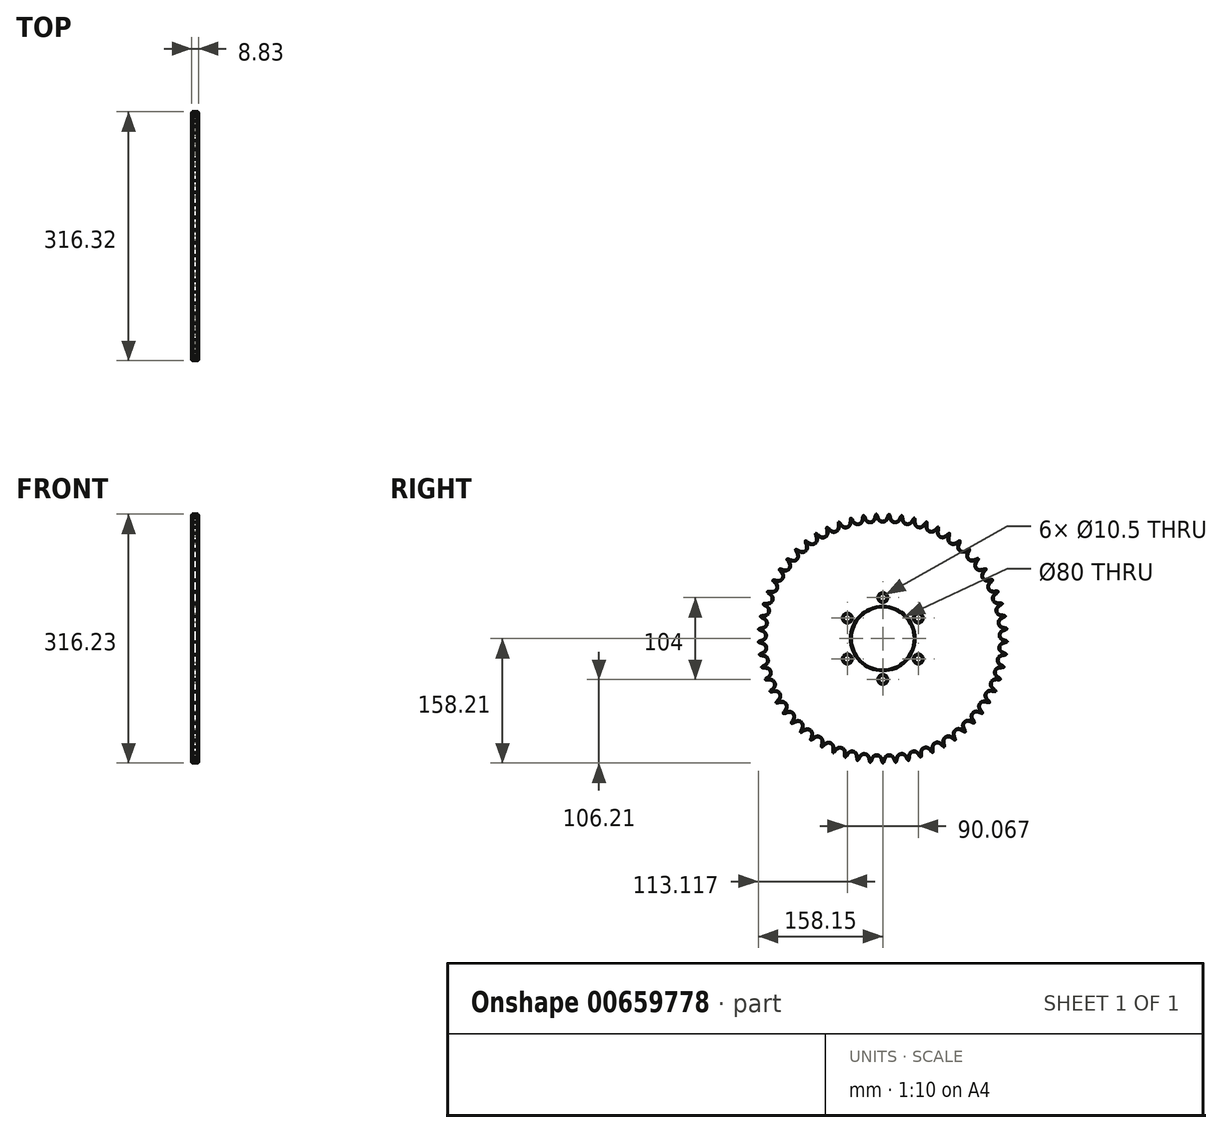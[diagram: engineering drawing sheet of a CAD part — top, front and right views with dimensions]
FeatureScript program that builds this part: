
annotation { "Feature Type Name" : "Feature", "Feature Type Description" : "" }
export const myFeature = defineFeature(function(context is Context, id is Id, definition is map)
    precondition{}
    {
        {
            var Q0;
            Q0=qCreatedBy(makeId("Front.planeOp"),FACE);
            var sketch = newSketch(context, id + "F0", { "sketchPlane" : qUnion([Q0])});
            skLineSegment(sketch, "E0", {"start": v(0, 0) * mm, "end": v(26.72, 0) * mm, "construction": true});
            skLineSegment(sketch, "E1.bottom", {"start": v(0, 40) * mm, "end": v(8.83, 40) * mm});
            skLineSegment(sketch, "E1.top", {"start": v(0, 158.2) * mm, "end": v(8.83, 158.2) * mm});
            skLineSegment(sketch, "E1.left", {"start": v(0, 40) * mm, "end": v(0, 158.2) * mm});
            skLineSegment(sketch, "E1.right", {"start": v(8.83, 40) * mm, "end": v(8.82, 158.2) * mm});
            skLineSegment(sketch, "E2.MirrorCS", {"start": v(8.83, -40) * mm, "end": v(8.83, -158.2) * mm});
            skLineSegment(sketch, "E3.MirrorCS", {"start": v(0, -158.2) * mm, "end": v(8.83, -158.2) * mm});
            skLineSegment(sketch, "E4.MirrorCS", {"start": v(0, -40) * mm, "end": v(8.83, -40) * mm});
            skLineSegment(sketch, "E5.MirrorCS", {"start": v(0, -40) * mm, "end": v(0, -158.2) * mm});
            skSolve(sketch);
        }
        {
            var Q0;
            Q0=makeQuery(id+"F0.imprint","IMPRINT",FACE,{"disambiguationData":[TD([[makeQuery(id+"F0.imprint","IMPRINT",EDGE,{"derivedFrom":sQuery(id+"F0.wireOp",EDGE,"E1.bottom")}),1.0]])]});
            var Q1;
            Q1=sQuery(id+"F0.wireOp",EDGE,"E0");
            revolve(context, id + "F1", {"entities" : qUnion([Q0]), "axis" : qUnion([Q1]), "revolveType" : RevolveType.FULL});
        }
        {
            var Q0;
            Q0=makeQuery(id+"F1.opRevolve","SWEPT_FACE",FACE,{"disambiguationData":[OSD([sQuery(id+"F0.wireOp",EDGE,"E1.left")])]});
            var sketch = newSketch(context, id + "F2", { "sketchPlane" : qUnion([Q0])});
            skCircle(sketch, "E6", {"center": v(0.24, 0) * mm, "radius": 158.2 * mm, "construction": true});
            skCircle(sketch, "E7", {"center": v(0.24, 0) * mm, "radius": 154.2 * mm, "construction": true});
            skCircle(sketch, "E8", {"center": v(0.24, 0) * mm, "radius": 149.03 * mm, "construction": true});
            skLineSegment(sketch, "E9", {"start": v(0.24, 0) * mm, "end": v(0.24, 107.73) * mm, "construction": true});
            skLineSegment(sketch, "E10", {"start": v(-4.24, 86.97) * mm, "end": v(0.24, 0) * mm, "construction": true});
            skLineSegment(sketch, "E11", {"start": v(0, 0) * mm, "end": v(0, 107.73) * mm, "construction": true});
            skLineSegment(sketch, "E12", {"start": v(0, 154.19) * mm, "end": v(-70.6, 102.92) * mm, "construction": true});
            skLineSegment(sketch, "E13", {"start": v(0, 154.19) * mm, "end": v(6.58, 158.97) * mm, "construction": true});
            skLineSegment(sketch, "E14", {"start": v(6.58, 158.97) * mm, "end": v(-48.08, 140.25) * mm, "construction": true});
            skLineSegment(sketch, "E15", {"start": v(-5.99, 154.66) * mm, "end": v(-6.34, 155.68) * mm});
            skLineSegment(sketch, "E16", {"start": v(-6.34, 155.68) * mm, "end": v(-12.58, 153.54) * mm, "construction": true});
            skArc(sketch, "E17", {"start": v(-5.99, 154.66) * mm, "mid": v(-5.21, 152.84) * mm, "end": v(-4.17, 151.16) * mm});
            skArc(sketch, "E18", {"start": v(-4.17, 151.16) * mm, "mid": v(18.37, 165.09) * mm, "end": v(-5.99, 154.66) * mm, "construction": true});
            skArc(sketch, "E19", {"start": v(0, 149.03) * mm, "mid": v(2.34, 158.78) * mm, "end": v(-4.17, 151.16) * mm, "construction": true});
            skArc(sketch, "E20", {"start": v(-4.17, 151.16) * mm, "mid": v(-2.34, 149.6) * mm, "end": v(0, 149.03) * mm});
            skLineSegment(sketch, "E21", {"start": v(0, 149.03) * mm, "end": v(0.24, 149.03) * mm});
            skArc(sketch, "E22", {"start": v(-7.92, 158.21) * mm, "mid": v(-18.18, 150.05) * mm, "end": v(-6.34, 155.68) * mm, "construction": true});
            skArc(sketch, "E23", {"start": v(-6.34, 155.68) * mm, "mid": v(-6.98, 157.04) * mm, "end": v(-7.92, 158.21) * mm});
            skArc(sketch, "E24.MirrorCS", {"start": v(4.65, 151.16) * mm, "mid": v(2.82, 149.6) * mm, "end": v(0.48, 149.03) * mm});
            skArc(sketch, "E25.MirrorCS", {"start": v(6.47, 154.66) * mm, "mid": v(5.69, 152.84) * mm, "end": v(4.65, 151.16) * mm});
            skLineSegment(sketch, "E26.MirrorCS", {"start": v(6.47, 154.66) * mm, "end": v(6.81, 155.68) * mm});
            skArc(sketch, "E27.MirrorCS", {"start": v(6.81, 155.68) * mm, "mid": v(7.46, 157.04) * mm, "end": v(8.4, 158.21) * mm});
            skLineSegment(sketch, "E28.MirrorCS", {"start": v(0.48, 149.03) * mm, "end": v(0.24, 149.03) * mm});
            skArc(sketch, "E29.1.0", {"start": v(-22.31, 154.2) * mm, "mid": v(-23.1, 155.49) * mm, "end": v(-24.14, 156.56) * mm});
            skArc(sketch, "E29.1.1", {"start": v(-9.23, 155.56) * mm, "mid": v(-8.73, 156.97) * mm, "end": v(-7.92, 158.23) * mm});
            skLineSegment(sketch, "E29.1.2", {"start": v(-9.47, 154.5) * mm, "end": v(-9.23, 155.56) * mm});
            skArc(sketch, "E29.1.3", {"start": v(-9.47, 154.5) * mm, "mid": v(-10.06, 152.62) * mm, "end": v(-10.92, 150.84) * mm});
            skArc(sketch, "E29.1.4", {"start": v(-10.92, 150.84) * mm, "mid": v(-12.58, 149.1) * mm, "end": v(-14.85, 148.3) * mm});
            skArc(sketch, "E29.1.5", {"start": v(-19.7, 149.93) * mm, "mid": v(-17.71, 148.56) * mm, "end": v(-15.32, 148.24) * mm});
            skArc(sketch, "E29.1.6", {"start": v(-21.86, 153.23) * mm, "mid": v(-20.9, 151.5) * mm, "end": v(-19.7, 149.93) * mm});
            skLineSegment(sketch, "E29.1.7", {"start": v(-21.86, 153.23) * mm, "end": v(-22.31, 154.2) * mm});
            skLineSegment(sketch, "E29.1.8", {"start": v(-14.85, 148.3) * mm, "end": v(-15.09, 148.27) * mm});
            skLineSegment(sketch, "E29.1.9", {"start": v(-15.32, 148.24) * mm, "end": v(-15.09, 148.27) * mm});
            skArc(sketch, "E29.2.0", {"start": v(-38.05, 151.1) * mm, "mid": v(-38.96, 152.29) * mm, "end": v(-40.11, 153.25) * mm});
            skArc(sketch, "E29.2.1", {"start": v(-25.17, 153.78) * mm, "mid": v(-24.82, 155.24) * mm, "end": v(-24.15, 156.58) * mm});
            skLineSegment(sketch, "E29.2.2", {"start": v(-25.3, 152.71) * mm, "end": v(-25.17, 153.78) * mm});
            skArc(sketch, "E29.2.3", {"start": v(-25.3, 152.71) * mm, "mid": v(-25.7, 150.78) * mm, "end": v(-26.37, 148.92) * mm});
            skArc(sketch, "E29.2.4", {"start": v(-26.37, 148.92) * mm, "mid": v(-27.84, 147.01) * mm, "end": v(-30.02, 145.98) * mm});
            skArc(sketch, "E29.2.5", {"start": v(-35, 147.11) * mm, "mid": v(-32.9, 145.96) * mm, "end": v(-30.49, 145.88) * mm});
            skArc(sketch, "E29.2.6", {"start": v(-37.5, 150.17) * mm, "mid": v(-36.37, 148.55) * mm, "end": v(-35, 147.11) * mm});
            skLineSegment(sketch, "E29.2.7", {"start": v(-37.5, 150.17) * mm, "end": v(-38.05, 151.1) * mm});
            skLineSegment(sketch, "E29.2.8", {"start": v(-30.02, 145.98) * mm, "end": v(-30.25, 145.93) * mm});
            skLineSegment(sketch, "E29.2.9", {"start": v(-30.49, 145.88) * mm, "end": v(-30.25, 145.93) * mm});
            skArc(sketch, "E29.3.0", {"start": v(-53.38, 146.38) * mm, "mid": v(-54.4, 147.47) * mm, "end": v(-55.66, 148.3) * mm});
            skArc(sketch, "E29.3.1", {"start": v(-40.85, 150.38) * mm, "mid": v(-40.65, 151.87) * mm, "end": v(-40.12, 153.27) * mm});
            skLineSegment(sketch, "E29.3.2", {"start": v(-40.88, 149.3) * mm, "end": v(-40.85, 150.38) * mm});
            skArc(sketch, "E29.3.3", {"start": v(-40.88, 149.3) * mm, "mid": v(-41.06, 147.33) * mm, "end": v(-41.54, 145.41) * mm});
            skArc(sketch, "E29.3.4", {"start": v(-41.54, 145.41) * mm, "mid": v(-42.81, 143.37) * mm, "end": v(-44.87, 142.12) * mm});
            skArc(sketch, "E29.3.5", {"start": v(-49.94, 142.73) * mm, "mid": v(-47.72, 141.8) * mm, "end": v(-45.32, 141.98) * mm});
            skArc(sketch, "E29.3.6", {"start": v(-52.74, 145.52) * mm, "mid": v(-51.45, 144.02) * mm, "end": v(-49.94, 142.73) * mm});
            skLineSegment(sketch, "E29.3.7", {"start": v(-52.74, 145.52) * mm, "end": v(-53.38, 146.38) * mm});
            skLineSegment(sketch, "E29.3.8", {"start": v(-44.87, 142.12) * mm, "end": v(-45.1, 142.05) * mm});
            skLineSegment(sketch, "E29.3.9", {"start": v(-45.32, 141.98) * mm, "end": v(-45.1, 142.05) * mm});
            skArc(sketch, "E29.4.0", {"start": v(-68.15, 140.11) * mm, "mid": v(-69.28, 141.1) * mm, "end": v(-70.61, 141.8) * mm});
            skArc(sketch, "E29.4.1", {"start": v(-56.1, 145.38) * mm, "mid": v(-56.05, 146.88) * mm, "end": v(-55.67, 148.33) * mm});
            skLineSegment(sketch, "E29.4.2", {"start": v(-56.01, 144.3) * mm, "end": v(-56.1, 145.38) * mm});
            skArc(sketch, "E29.4.3", {"start": v(-56.01, 144.3) * mm, "mid": v(-56, 142.33) * mm, "end": v(-56.27, 140.37) * mm});
            skArc(sketch, "E29.4.4", {"start": v(-56.27, 140.37) * mm, "mid": v(-57.33, 138.2) * mm, "end": v(-59.25, 136.75) * mm});
            skArc(sketch, "E29.4.5", {"start": v(-64.36, 136.84) * mm, "mid": v(-62.05, 136.14) * mm, "end": v(-59.68, 136.56) * mm});
            skArc(sketch, "E29.4.6", {"start": v(-67.42, 139.32) * mm, "mid": v(-65.98, 137.97) * mm, "end": v(-64.36, 136.84) * mm});
            skLineSegment(sketch, "E29.4.7", {"start": v(-67.42, 139.32) * mm, "end": v(-68.15, 140.11) * mm});
            skLineSegment(sketch, "E29.4.8", {"start": v(-59.25, 136.75) * mm, "end": v(-59.46, 136.66) * mm});
            skLineSegment(sketch, "E29.4.9", {"start": v(-59.68, 136.56) * mm, "end": v(-59.46, 136.66) * mm});
            skArc(sketch, "E29.5.0", {"start": v(-82.2, 132.36) * mm, "mid": v(-83.42, 133.23) * mm, "end": v(-84.82, 133.79) * mm});
            skArc(sketch, "E29.5.1", {"start": v(-70.75, 138.84) * mm, "mid": v(-70.86, 140.34) * mm, "end": v(-70.62, 141.82) * mm});
            skLineSegment(sketch, "E29.5.2", {"start": v(-70.55, 137.79) * mm, "end": v(-70.75, 138.84) * mm});
            skArc(sketch, "E29.5.3", {"start": v(-70.55, 137.79) * mm, "mid": v(-70.33, 135.82) * mm, "end": v(-70.4, 133.84) * mm});
            skArc(sketch, "E29.5.4", {"start": v(-70.4, 133.84) * mm, "mid": v(-71.23, 131.58) * mm, "end": v(-73, 129.94) * mm});
            skArc(sketch, "E29.5.5", {"start": v(-78.08, 129.5) * mm, "mid": v(-75.72, 129.04) * mm, "end": v(-73.4, 129.7) * mm});
            skArc(sketch, "E29.5.6", {"start": v(-81.4, 131.65) * mm, "mid": v(-79.82, 130.45) * mm, "end": v(-78.08, 129.5) * mm});
            skLineSegment(sketch, "E29.5.7", {"start": v(-81.4, 131.65) * mm, "end": v(-82.2, 132.36) * mm});
            skLineSegment(sketch, "E29.5.8", {"start": v(-73, 129.94) * mm, "end": v(-73.2, 129.82) * mm});
            skLineSegment(sketch, "E29.5.9", {"start": v(-73.4, 129.7) * mm, "end": v(-73.2, 129.82) * mm});
            skArc(sketch, "E29.6.0", {"start": v(-95.37, 123.21) * mm, "mid": v(-96.68, 123.94) * mm, "end": v(-98.12, 124.36) * mm});
            skArc(sketch, "E29.6.1", {"start": v(-84.65, 130.83) * mm, "mid": v(-84.91, 132.31) * mm, "end": v(-84.83, 133.8) * mm});
            skLineSegment(sketch, "E29.6.2", {"start": v(-84.35, 129.8) * mm, "end": v(-84.65, 130.83) * mm});
            skArc(sketch, "E29.6.3", {"start": v(-84.35, 129.8) * mm, "mid": v(-83.93, 127.87) * mm, "end": v(-83.8, 125.9) * mm});
            skArc(sketch, "E29.6.4", {"start": v(-83.8, 125.9) * mm, "mid": v(-84.38, 123.56) * mm, "end": v(-85.97, 121.74) * mm});
            skArc(sketch, "E29.6.5", {"start": v(-90.99, 120.78) * mm, "mid": v(-88.59, 120.57) * mm, "end": v(-86.35, 121.47) * mm});
            skArc(sketch, "E29.6.6", {"start": v(-94.5, 122.58) * mm, "mid": v(-92.8, 121.55) * mm, "end": v(-90.99, 120.78) * mm});
            skLineSegment(sketch, "E29.6.7", {"start": v(-94.5, 122.58) * mm, "end": v(-95.37, 123.21) * mm});
            skLineSegment(sketch, "E29.6.8", {"start": v(-85.97, 121.74) * mm, "end": v(-86.16, 121.6) * mm});
            skLineSegment(sketch, "E29.6.9", {"start": v(-86.35, 121.47) * mm, "end": v(-86.16, 121.6) * mm});
            skArc(sketch, "E29.7.0", {"start": v(-107.53, 112.75) * mm, "mid": v(-108.91, 113.34) * mm, "end": v(-110.39, 113.61) * mm});
            skArc(sketch, "E29.7.1", {"start": v(-97.65, 121.43) * mm, "mid": v(-98.06, 122.88) * mm, "end": v(-98.14, 124.38) * mm});
            skLineSegment(sketch, "E29.7.2", {"start": v(-97.24, 120.44) * mm, "end": v(-97.65, 121.43) * mm});
            skArc(sketch, "E29.7.3", {"start": v(-97.24, 120.44) * mm, "mid": v(-96.63, 118.56) * mm, "end": v(-96.3, 116.6) * mm});
            skArc(sketch, "E29.7.4", {"start": v(-96.3, 116.6) * mm, "mid": v(-96.64, 114.23) * mm, "end": v(-98.03, 112.26) * mm});
            skArc(sketch, "E29.7.5", {"start": v(-102.92, 110.79) * mm, "mid": v(-100.52, 110.82) * mm, "end": v(-98.39, 111.94) * mm});
            skArc(sketch, "E29.7.6", {"start": v(-106.6, 112.22) * mm, "mid": v(-104.81, 111.37) * mm, "end": v(-102.92, 110.79) * mm});
            skLineSegment(sketch, "E29.7.7", {"start": v(-106.6, 112.22) * mm, "end": v(-107.53, 112.75) * mm});
            skLineSegment(sketch, "E29.7.8", {"start": v(-98.03, 112.26) * mm, "end": v(-98.2, 112.1) * mm});
            skLineSegment(sketch, "E29.7.9", {"start": v(-98.39, 111.94) * mm, "end": v(-98.2, 112.1) * mm});
            skArc(sketch, "E29.8.0", {"start": v(-118.56, 101.1) * mm, "mid": v(-119.99, 101.55) * mm, "end": v(-121.49, 101.66) * mm});
            skArc(sketch, "E29.8.1", {"start": v(-109.62, 110.75) * mm, "mid": v(-110.18, 112.14) * mm, "end": v(-110.4, 113.63) * mm});
            skLineSegment(sketch, "E29.8.2", {"start": v(-109.11, 109.8) * mm, "end": v(-109.62, 110.75) * mm});
            skArc(sketch, "E29.8.3", {"start": v(-109.11, 109.8) * mm, "mid": v(-108.3, 108) * mm, "end": v(-107.78, 106.1) * mm});
            skArc(sketch, "E29.8.4", {"start": v(-107.78, 106.1) * mm, "mid": v(-107.87, 103.68) * mm, "end": v(-109.05, 101.58) * mm});
            skArc(sketch, "E29.8.5", {"start": v(-113.77, 99.62) * mm, "mid": v(-111.38, 99.9) * mm, "end": v(-109.37, 101.24) * mm});
            skArc(sketch, "E29.8.6", {"start": v(-117.57, 100.66) * mm, "mid": v(-115.7, 100) * mm, "end": v(-113.77, 99.62) * mm});
            skLineSegment(sketch, "E29.8.7", {"start": v(-117.57, 100.66) * mm, "end": v(-118.56, 101.1) * mm});
            skLineSegment(sketch, "E29.8.8", {"start": v(-109.05, 101.58) * mm, "end": v(-109.21, 101.41) * mm});
            skLineSegment(sketch, "E29.8.9", {"start": v(-109.37, 101.24) * mm, "end": v(-109.21, 101.41) * mm});
            skArc(sketch, "E29.9.0", {"start": v(-128.32, 88.37) * mm, "mid": v(-129.8, 88.67) * mm, "end": v(-131.3, 88.63) * mm});
            skArc(sketch, "E29.9.1", {"start": v(-120.43, 98.9) * mm, "mid": v(-121.13, 100.22) * mm, "end": v(-121.5, 101.67) * mm});
            skLineSegment(sketch, "E29.9.2", {"start": v(-119.82, 98) * mm, "end": v(-120.43, 98.9) * mm});
            skArc(sketch, "E29.9.3", {"start": v(-119.82, 98) * mm, "mid": v(-118.84, 96.29) * mm, "end": v(-118.12, 94.45) * mm});
            skArc(sketch, "E29.9.4", {"start": v(-118.12, 94.45) * mm, "mid": v(-117.96, 92.04) * mm, "end": v(-118.92, 89.83) * mm});
            skArc(sketch, "E29.9.5", {"start": v(-123.4, 87.4) * mm, "mid": v(-121.06, 87.92) * mm, "end": v(-119.2, 89.45) * mm});
            skArc(sketch, "E29.9.6", {"start": v(-127.3, 88.04) * mm, "mid": v(-125.38, 87.57) * mm, "end": v(-123.4, 87.4) * mm});
            skLineSegment(sketch, "E29.9.7", {"start": v(-127.3, 88.04) * mm, "end": v(-128.32, 88.37) * mm});
            skLineSegment(sketch, "E29.9.8", {"start": v(-118.92, 89.83) * mm, "end": v(-119.06, 89.64) * mm});
            skLineSegment(sketch, "E29.9.9", {"start": v(-119.2, 89.45) * mm, "end": v(-119.06, 89.64) * mm});
            skArc(sketch, "E29.10.0", {"start": v(-136.73, 74.7) * mm, "mid": v(-138.22, 74.85) * mm, "end": v(-139.71, 74.66) * mm});
            skArc(sketch, "E29.10.1", {"start": v(-129.96, 85.98) * mm, "mid": v(-130.79, 87.24) * mm, "end": v(-131.32, 88.64) * mm});
            skLineSegment(sketch, "E29.10.2", {"start": v(-129.27, 85.16) * mm, "end": v(-129.96, 85.98) * mm});
            skArc(sketch, "E29.10.3", {"start": v(-129.27, 85.16) * mm, "mid": v(-128.1, 83.56) * mm, "end": v(-127.2, 81.8) * mm});
            skArc(sketch, "E29.10.4", {"start": v(-127.2, 81.8) * mm, "mid": v(-126.8, 79.43) * mm, "end": v(-127.52, 77.13) * mm});
            skArc(sketch, "E29.10.5", {"start": v(-131.74, 74.24) * mm, "mid": v(-129.46, 75) * mm, "end": v(-127.77, 76.72) * mm});
            skArc(sketch, "E29.10.6", {"start": v(-135.68, 74.48) * mm, "mid": v(-133.72, 74.22) * mm, "end": v(-131.74, 74.24) * mm});
            skLineSegment(sketch, "E29.10.7", {"start": v(-135.68, 74.48) * mm, "end": v(-136.73, 74.7) * mm});
            skLineSegment(sketch, "E29.10.8", {"start": v(-127.52, 77.13) * mm, "end": v(-127.65, 76.93) * mm});
            skLineSegment(sketch, "E29.10.9", {"start": v(-127.77, 76.72) * mm, "end": v(-127.65, 76.93) * mm});
            skArc(sketch, "E29.11.0", {"start": v(-143.69, 60.25) * mm, "mid": v(-145.19, 60.25) * mm, "end": v(-146.65, 59.9) * mm});
            skArc(sketch, "E29.11.1", {"start": v(-138.11, 72.17) * mm, "mid": v(-139.07, 73.32) * mm, "end": v(-139.73, 74.67) * mm});
            skLineSegment(sketch, "E29.11.2", {"start": v(-137.34, 71.42) * mm, "end": v(-138.11, 72.17) * mm});
            skArc(sketch, "E29.11.3", {"start": v(-137.34, 71.42) * mm, "mid": v(-136.02, 69.94) * mm, "end": v(-134.94, 68.29) * mm});
            skArc(sketch, "E29.11.4", {"start": v(-134.94, 68.29) * mm, "mid": v(-134.3, 65.97) * mm, "end": v(-134.78, 63.6) * mm});
            skArc(sketch, "E29.11.5", {"start": v(-138.68, 60.3) * mm, "mid": v(-136.48, 61.3) * mm, "end": v(-134.98, 63.18) * mm});
            skArc(sketch, "E29.11.6", {"start": v(-142.62, 60.14) * mm, "mid": v(-140.64, 60.07) * mm, "end": v(-138.68, 60.3) * mm});
            skLineSegment(sketch, "E29.11.7", {"start": v(-142.62, 60.14) * mm, "end": v(-143.69, 60.25) * mm});
            skLineSegment(sketch, "E29.11.8", {"start": v(-134.78, 63.6) * mm, "end": v(-134.88, 63.4) * mm});
            skLineSegment(sketch, "E29.11.9", {"start": v(-134.98, 63.18) * mm, "end": v(-134.88, 63.4) * mm});
            skArc(sketch, "E29.12.0", {"start": v(-149.12, 45.16) * mm, "mid": v(-150.61, 45) * mm, "end": v(-152.03, 44.5) * mm});
            skArc(sketch, "E29.12.1", {"start": v(-144.8, 57.58) * mm, "mid": v(-145.87, 58.64) * mm, "end": v(-146.67, 59.9) * mm});
            skLineSegment(sketch, "E29.12.2", {"start": v(-143.95, 56.92) * mm, "end": v(-144.8, 57.58) * mm});
            skArc(sketch, "E29.12.3", {"start": v(-143.95, 56.92) * mm, "mid": v(-142.5, 55.59) * mm, "end": v(-141.24, 54.05) * mm});
            skArc(sketch, "E29.12.4", {"start": v(-141.24, 54.05) * mm, "mid": v(-140.37, 51.8) * mm, "end": v(-140.6, 49.41) * mm});
            skArc(sketch, "E29.12.5", {"start": v(-144.14, 45.72) * mm, "mid": v(-142.06, 46.94) * mm, "end": v(-140.76, 48.96) * mm});
            skArc(sketch, "E29.12.6", {"start": v(-148.04, 45.16) * mm, "mid": v(-146.07, 45.3) * mm, "end": v(-144.14, 45.72) * mm});
            skLineSegment(sketch, "E29.12.7", {"start": v(-148.04, 45.16) * mm, "end": v(-149.12, 45.16) * mm});
            skLineSegment(sketch, "E29.12.8", {"start": v(-140.6, 49.41) * mm, "end": v(-140.68, 49.19) * mm});
            skLineSegment(sketch, "E29.12.9", {"start": v(-140.76, 48.96) * mm, "end": v(-140.68, 49.19) * mm});
            skArc(sketch, "E29.13.0", {"start": v(-152.97, 29.59) * mm, "mid": v(-154.44, 29.27) * mm, "end": v(-155.8, 28.63) * mm});
            skArc(sketch, "E29.13.1", {"start": v(-149.95, 42.39) * mm, "mid": v(-151.12, 43.33) * mm, "end": v(-152.05, 44.5) * mm});
            skLineSegment(sketch, "E29.13.2", {"start": v(-149.04, 41.82) * mm, "end": v(-149.95, 42.39) * mm});
            skArc(sketch, "E29.13.3", {"start": v(-149.04, 41.82) * mm, "mid": v(-147.45, 40.64) * mm, "end": v(-146.05, 39.24) * mm});
            skArc(sketch, "E29.13.4", {"start": v(-146.05, 39.24) * mm, "mid": v(-144.95, 37.1) * mm, "end": v(-144.94, 34.7) * mm});
            skArc(sketch, "E29.13.5", {"start": v(-148.08, 30.66) * mm, "mid": v(-146.14, 32.08) * mm, "end": v(-145.05, 34.23) * mm});
            skArc(sketch, "E29.13.6", {"start": v(-151.9, 29.7) * mm, "mid": v(-149.95, 30.03) * mm, "end": v(-148.08, 30.66) * mm});
            skLineSegment(sketch, "E29.13.7", {"start": v(-151.9, 29.7) * mm, "end": v(-152.97, 29.59) * mm});
            skLineSegment(sketch, "E29.13.8", {"start": v(-144.94, 34.7) * mm, "end": v(-145, 34.46) * mm});
            skLineSegment(sketch, "E29.13.9", {"start": v(-145.05, 34.23) * mm, "end": v(-145, 34.46) * mm});
            skArc(sketch, "E29.14.0", {"start": v(-155.2, 13.7) * mm, "mid": v(-156.63, 13.24) * mm, "end": v(-157.92, 12.46) * mm});
            skArc(sketch, "E29.14.1", {"start": v(-153.52, 26.75) * mm, "mid": v(-154.78, 27.56) * mm, "end": v(-155.82, 28.64) * mm});
            skLineSegment(sketch, "E29.14.2", {"start": v(-152.55, 26.27) * mm, "end": v(-153.52, 26.75) * mm});
            skArc(sketch, "E29.14.3", {"start": v(-152.55, 26.27) * mm, "mid": v(-150.85, 25.27) * mm, "end": v(-149.31, 24.02) * mm});
            skArc(sketch, "E29.14.4", {"start": v(-149.31, 24.02) * mm, "mid": v(-148, 22) * mm, "end": v(-147.74, 19.6) * mm});
            skArc(sketch, "E29.14.5", {"start": v(-150.45, 15.27) * mm, "mid": v(-148.66, 16.89) * mm, "end": v(-147.8, 19.14) * mm});
            skArc(sketch, "E29.14.6", {"start": v(-154.15, 13.92) * mm, "mid": v(-152.25, 14.46) * mm, "end": v(-150.45, 15.27) * mm});
            skLineSegment(sketch, "E29.14.7", {"start": v(-154.15, 13.92) * mm, "end": v(-155.2, 13.7) * mm});
            skLineSegment(sketch, "E29.14.8", {"start": v(-147.74, 19.6) * mm, "end": v(-147.77, 19.37) * mm});
            skLineSegment(sketch, "E29.14.9", {"start": v(-147.8, 19.14) * mm, "end": v(-147.77, 19.37) * mm});
            skArc(sketch, "E29.15.0", {"start": v(-155.8, -2.33) * mm, "mid": v(-157.16, -2.94) * mm, "end": v(-158.36, -3.84) * mm});
            skArc(sketch, "E29.15.1", {"start": v(-155.45, 10.82) * mm, "mid": v(-156.8, 11.5) * mm, "end": v(-157.94, 12.46) * mm});
            skLineSegment(sketch, "E29.15.2", {"start": v(-154.44, 10.45) * mm, "end": v(-155.45, 10.82) * mm});
            skArc(sketch, "E29.15.3", {"start": v(-154.44, 10.45) * mm, "mid": v(-152.65, 9.62) * mm, "end": v(-151, 8.54) * mm});
            skArc(sketch, "E29.15.4", {"start": v(-151, 8.54) * mm, "mid": v(-149.47, 6.67) * mm, "end": v(-148.97, 4.31) * mm});
            skArc(sketch, "E29.15.5", {"start": v(-151.22, -0.28) * mm, "mid": v(-149.6, 1.51) * mm, "end": v(-148.99, 3.84) * mm});
            skArc(sketch, "E29.15.6", {"start": v(-154.77, -2) * mm, "mid": v(-152.93, -1.27) * mm, "end": v(-151.22, -0.28) * mm});
            skLineSegment(sketch, "E29.15.7", {"start": v(-154.77, -2) * mm, "end": v(-155.8, -2.33) * mm});
            skLineSegment(sketch, "E29.15.8", {"start": v(-148.97, 4.31) * mm, "end": v(-148.98, 4.08) * mm});
            skLineSegment(sketch, "E29.15.9", {"start": v(-148.99, 3.84) * mm, "end": v(-148.98, 4.08) * mm});
            skArc(sketch, "E29.16.0", {"start": v(-154.73, -18.33) * mm, "mid": v(-156.03, -19.08) * mm, "end": v(-157.13, -20.1) * mm});
            skArc(sketch, "E29.16.1", {"start": v(-155.74, -5.22) * mm, "mid": v(-157.14, -4.68) * mm, "end": v(-158.39, -3.84) * mm});
            skLineSegment(sketch, "E29.16.2", {"start": v(-154.7, -5.49) * mm, "end": v(-155.74, -5.22) * mm});
            skArc(sketch, "E29.16.3", {"start": v(-154.7, -5.49) * mm, "mid": v(-152.83, -6.13) * mm, "end": v(-151.07, -7.03) * mm});
            skArc(sketch, "E29.16.4", {"start": v(-151.07, -7.03) * mm, "mid": v(-149.37, -8.74) * mm, "end": v(-148.63, -11.03) * mm});
            skArc(sketch, "E29.16.5", {"start": v(-150.39, -15.82) * mm, "mid": v(-148.97, -13.88) * mm, "end": v(-148.6, -11.5) * mm});
            skArc(sketch, "E29.16.6", {"start": v(-153.74, -17.9) * mm, "mid": v(-151.99, -17) * mm, "end": v(-150.39, -15.82) * mm});
            skLineSegment(sketch, "E29.16.7", {"start": v(-153.74, -17.9) * mm, "end": v(-154.73, -18.33) * mm});
            skLineSegment(sketch, "E29.16.8", {"start": v(-148.63, -11.03) * mm, "end": v(-148.6, -11.26) * mm});
            skLineSegment(sketch, "E29.16.9", {"start": v(-148.6, -11.5) * mm, "end": v(-148.6, -11.26) * mm});
            skArc(sketch, "E29.17.0", {"start": v(-152.02, -34.15) * mm, "mid": v(-153.24, -35.02) * mm, "end": v(-154.23, -36.15) * mm});
            skArc(sketch, "E29.17.1", {"start": v(-154.38, -21.2) * mm, "mid": v(-155.83, -20.82) * mm, "end": v(-157.15, -20.1) * mm});
            skLineSegment(sketch, "E29.17.2", {"start": v(-153.32, -21.37) * mm, "end": v(-154.38, -21.2) * mm});
            skArc(sketch, "E29.17.3", {"start": v(-153.32, -21.37) * mm, "mid": v(-151.39, -21.8) * mm, "end": v(-149.55, -22.53) * mm});
            skArc(sketch, "E29.17.4", {"start": v(-149.55, -22.53) * mm, "mid": v(-147.68, -24.05) * mm, "end": v(-146.7, -26.25) * mm});
            skArc(sketch, "E29.17.5", {"start": v(-147.96, -31.2) * mm, "mid": v(-146.75, -29.12) * mm, "end": v(-146.62, -26.72) * mm});
            skArc(sketch, "E29.17.6", {"start": v(-151.08, -33.62) * mm, "mid": v(-149.43, -32.53) * mm, "end": v(-147.96, -31.2) * mm});
            skLineSegment(sketch, "E29.17.7", {"start": v(-151.08, -33.62) * mm, "end": v(-152.02, -34.15) * mm});
            skLineSegment(sketch, "E29.17.8", {"start": v(-146.7, -26.25) * mm, "end": v(-146.66, -26.48) * mm});
            skLineSegment(sketch, "E29.17.9", {"start": v(-146.62, -26.72) * mm, "end": v(-146.66, -26.48) * mm});
            skArc(sketch, "E29.18.0", {"start": v(-147.7, -49.6) * mm, "mid": v(-148.83, -50.6) * mm, "end": v(-149.7, -51.82) * mm});
            skArc(sketch, "E29.18.1", {"start": v(-151.38, -36.97) * mm, "mid": v(-152.86, -36.73) * mm, "end": v(-154.25, -36.16) * mm});
            skLineSegment(sketch, "E29.18.2", {"start": v(-150.3, -37.02) * mm, "end": v(-151.38, -36.97) * mm});
            skArc(sketch, "E29.18.3", {"start": v(-150.3, -37.02) * mm, "mid": v(-148.34, -37.26) * mm, "end": v(-146.44, -37.79) * mm});
            skArc(sketch, "E29.18.4", {"start": v(-146.44, -37.79) * mm, "mid": v(-144.42, -39.1) * mm, "end": v(-143.23, -41.2) * mm});
            skArc(sketch, "E29.18.5", {"start": v(-143.97, -46.25) * mm, "mid": v(-142.98, -44.06) * mm, "end": v(-143.1, -41.65) * mm});
            skArc(sketch, "E29.18.6", {"start": v(-146.83, -48.98) * mm, "mid": v(-145.3, -47.72) * mm, "end": v(-143.97, -46.25) * mm});
            skLineSegment(sketch, "E29.18.7", {"start": v(-146.83, -48.98) * mm, "end": v(-147.7, -49.6) * mm});
            skLineSegment(sketch, "E29.18.8", {"start": v(-143.23, -41.2) * mm, "end": v(-143.16, -41.42) * mm});
            skLineSegment(sketch, "E29.18.9", {"start": v(-143.1, -41.65) * mm, "end": v(-143.16, -41.42) * mm});
            skArc(sketch, "E29.19.0", {"start": v(-141.82, -64.52) * mm, "mid": v(-142.84, -65.63) * mm, "end": v(-143.57, -66.94) * mm});
            skArc(sketch, "E29.19.1", {"start": v(-146.78, -52.34) * mm, "mid": v(-148.28, -52.25) * mm, "end": v(-149.72, -51.83) * mm});
            skLineSegment(sketch, "E29.19.2", {"start": v(-145.7, -52.28) * mm, "end": v(-146.78, -52.34) * mm});
            skArc(sketch, "E29.19.3", {"start": v(-145.7, -52.28) * mm, "mid": v(-143.73, -52.31) * mm, "end": v(-141.77, -52.64) * mm});
            skArc(sketch, "E29.19.4", {"start": v(-141.77, -52.64) * mm, "mid": v(-139.64, -53.75) * mm, "end": v(-138.23, -55.7) * mm});
            skArc(sketch, "E29.19.5", {"start": v(-138.45, -60.81) * mm, "mid": v(-137.7, -58.53) * mm, "end": v(-138.05, -56.15) * mm});
            skArc(sketch, "E29.19.6", {"start": v(-141.01, -63.81) * mm, "mid": v(-139.62, -62.4) * mm, "end": v(-138.45, -60.81) * mm});
            skLineSegment(sketch, "E29.19.7", {"start": v(-141.01, -63.81) * mm, "end": v(-141.82, -64.52) * mm});
            skLineSegment(sketch, "E29.19.8", {"start": v(-138.23, -55.7) * mm, "end": v(-138.14, -55.93) * mm});
            skLineSegment(sketch, "E29.19.9", {"start": v(-138.05, -56.15) * mm, "end": v(-138.14, -55.93) * mm});
            skArc(sketch, "E29.20.0", {"start": v(-134.44, -78.76) * mm, "mid": v(-135.33, -79.97) * mm, "end": v(-135.93, -81.34) * mm});
            skArc(sketch, "E29.20.1", {"start": v(-140.62, -67.15) * mm, "mid": v(-142.12, -67.22) * mm, "end": v(-143.6, -66.95) * mm});
            skLineSegment(sketch, "E29.20.2", {"start": v(-139.56, -66.98) * mm, "end": v(-140.62, -67.15) * mm});
            skArc(sketch, "E29.20.3", {"start": v(-139.56, -66.98) * mm, "mid": v(-137.58, -66.81) * mm, "end": v(-135.61, -66.94) * mm});
            skArc(sketch, "E29.20.4", {"start": v(-135.61, -66.94) * mm, "mid": v(-133.37, -67.82) * mm, "end": v(-131.77, -69.62) * mm});
            skArc(sketch, "E29.20.5", {"start": v(-131.47, -74.72) * mm, "mid": v(-130.95, -72.37) * mm, "end": v(-131.55, -70.04) * mm});
            skArc(sketch, "E29.20.6", {"start": v(-133.7, -77.97) * mm, "mid": v(-132.46, -76.43) * mm, "end": v(-131.47, -74.72) * mm});
            skLineSegment(sketch, "E29.20.7", {"start": v(-133.7, -77.97) * mm, "end": v(-134.44, -78.76) * mm});
            skLineSegment(sketch, "E29.20.8", {"start": v(-131.77, -69.62) * mm, "end": v(-131.66, -69.83) * mm});
            skLineSegment(sketch, "E29.20.9", {"start": v(-131.55, -70.04) * mm, "end": v(-131.66, -69.83) * mm});
            skArc(sketch, "E29.21.0", {"start": v(-125.63, -92.17) * mm, "mid": v(-126.4, -93.46) * mm, "end": v(-126.84, -94.89) * mm});
            skArc(sketch, "E29.21.1", {"start": v(-132.97, -81.25) * mm, "mid": v(-134.45, -81.48) * mm, "end": v(-135.95, -81.36) * mm});
            skLineSegment(sketch, "E29.21.2", {"start": v(-131.93, -80.97) * mm, "end": v(-132.97, -81.25) * mm});
            skArc(sketch, "E29.21.3", {"start": v(-131.93, -80.97) * mm, "mid": v(-129.99, -80.6) * mm, "end": v(-128, -80.53) * mm});
            skArc(sketch, "E29.21.4", {"start": v(-128, -80.53) * mm, "mid": v(-125.69, -81.17) * mm, "end": v(-123.92, -82.8) * mm});
            skArc(sketch, "E29.21.5", {"start": v(-123.09, -87.85) * mm, "mid": v(-122.81, -85.45) * mm, "end": v(-123.65, -83.2) * mm});
            skArc(sketch, "E29.21.6", {"start": v(-124.98, -91.3) * mm, "mid": v(-123.9, -89.65) * mm, "end": v(-123.09, -87.85) * mm});
            skLineSegment(sketch, "E29.21.7", {"start": v(-124.98, -91.3) * mm, "end": v(-125.63, -92.17) * mm});
            skLineSegment(sketch, "E29.21.8", {"start": v(-123.92, -82.8) * mm, "end": v(-123.78, -83) * mm});
            skLineSegment(sketch, "E29.21.9", {"start": v(-123.65, -83.2) * mm, "end": v(-123.78, -83) * mm});
            skArc(sketch, "E29.22.0", {"start": v(-115.48, -104.6) * mm, "mid": v(-116.11, -105.96) * mm, "end": v(-116.41, -107.43) * mm});
            skArc(sketch, "E29.22.1", {"start": v(-123.9, -94.5) * mm, "mid": v(-125.36, -94.87) * mm, "end": v(-126.86, -94.9) * mm});
            skLineSegment(sketch, "E29.22.2", {"start": v(-122.9, -94.11) * mm, "end": v(-123.9, -94.5) * mm});
            skArc(sketch, "E29.22.3", {"start": v(-122.9, -94.11) * mm, "mid": v(-121, -93.54) * mm, "end": v(-119.05, -93.26) * mm});
            skArc(sketch, "E29.22.4", {"start": v(-119.05, -93.26) * mm, "mid": v(-116.68, -93.67) * mm, "end": v(-114.75, -95.1) * mm});
            skArc(sketch, "E29.22.5", {"start": v(-113.4, -100.04) * mm, "mid": v(-113.37, -97.63) * mm, "end": v(-114.44, -95.47) * mm});
            skArc(sketch, "E29.22.6", {"start": v(-114.93, -103.68) * mm, "mid": v(-114.03, -101.91) * mm, "end": v(-113.4, -100.04) * mm});
            skLineSegment(sketch, "E29.22.7", {"start": v(-114.93, -103.68) * mm, "end": v(-115.48, -104.6) * mm});
            skLineSegment(sketch, "E29.22.8", {"start": v(-114.75, -95.1) * mm, "end": v(-114.6, -95.29) * mm});
            skLineSegment(sketch, "E29.22.9", {"start": v(-114.44, -95.47) * mm, "end": v(-114.6, -95.29) * mm});
            skArc(sketch, "E29.23.0", {"start": v(-104.12, -115.91) * mm, "mid": v(-104.6, -117.33) * mm, "end": v(-104.75, -118.83) * mm});
            skArc(sketch, "E29.23.1", {"start": v(-113.54, -106.73) * mm, "mid": v(-114.94, -107.26) * mm, "end": v(-116.43, -107.44) * mm});
            skLineSegment(sketch, "E29.23.2", {"start": v(-112.58, -106.25) * mm, "end": v(-113.54, -106.73) * mm});
            skArc(sketch, "E29.23.3", {"start": v(-112.58, -106.25) * mm, "mid": v(-110.75, -105.5) * mm, "end": v(-108.83, -105.01) * mm});
            skArc(sketch, "E29.23.4", {"start": v(-108.83, -105.01) * mm, "mid": v(-106.43, -105.17) * mm, "end": v(-104.36, -106.4) * mm});
            skArc(sketch, "E29.23.5", {"start": v(-102.51, -111.17) * mm, "mid": v(-102.73, -108.77) * mm, "end": v(-104.02, -106.73) * mm});
            skArc(sketch, "E29.23.6", {"start": v(-103.66, -114.94) * mm, "mid": v(-102.94, -113.1) * mm, "end": v(-102.51, -111.17) * mm});
            skLineSegment(sketch, "E29.23.7", {"start": v(-103.66, -114.94) * mm, "end": v(-104.12, -115.91) * mm});
            skLineSegment(sketch, "E29.23.8", {"start": v(-104.36, -106.4) * mm, "end": v(-104.19, -106.57) * mm});
            skLineSegment(sketch, "E29.23.9", {"start": v(-104.02, -106.73) * mm, "end": v(-104.19, -106.57) * mm});
            skArc(sketch, "E29.24.0", {"start": v(-91.65, -126) * mm, "mid": v(-91.98, -127.47) * mm, "end": v(-91.98, -128.97) * mm});
            skArc(sketch, "E29.24.1", {"start": v(-101.96, -117.84) * mm, "mid": v(-103.3, -118.5) * mm, "end": v(-104.77, -118.85) * mm});
            skLineSegment(sketch, "E29.24.2", {"start": v(-101.05, -117.26) * mm, "end": v(-101.96, -117.84) * mm});
            skArc(sketch, "E29.24.3", {"start": v(-101.05, -117.26) * mm, "mid": v(-99.32, -116.32) * mm, "end": v(-97.46, -115.64) * mm});
            skArc(sketch, "E29.24.4", {"start": v(-97.46, -115.64) * mm, "mid": v(-95.05, -115.55) * mm, "end": v(-92.87, -116.57) * mm});
            skArc(sketch, "E29.24.5", {"start": v(-90.54, -121.12) * mm, "mid": v(-91, -118.75) * mm, "end": v(-92.5, -116.86) * mm});
            skArc(sketch, "E29.24.6", {"start": v(-91.29, -125) * mm, "mid": v(-90.77, -123.08) * mm, "end": v(-90.54, -121.12) * mm});
            skLineSegment(sketch, "E29.24.7", {"start": v(-91.29, -125) * mm, "end": v(-91.65, -126) * mm});
            skLineSegment(sketch, "E29.24.8", {"start": v(-92.87, -116.57) * mm, "end": v(-92.68, -116.71) * mm});
            skLineSegment(sketch, "E29.24.9", {"start": v(-92.5, -116.86) * mm, "end": v(-92.68, -116.71) * mm});
            skArc(sketch, "E29.25.0", {"start": v(-78.2, -134.76) * mm, "mid": v(-78.39, -136.25) * mm, "end": v(-78.23, -137.74) * mm});
            skArc(sketch, "E29.25.1", {"start": v(-89.3, -127.7) * mm, "mid": v(-90.57, -128.5) * mm, "end": v(-92, -128.99) * mm});
            skLineSegment(sketch, "E29.25.2", {"start": v(-88.46, -127.03) * mm, "end": v(-89.3, -127.7) * mm});
            skArc(sketch, "E29.25.3", {"start": v(-88.46, -127.03) * mm, "mid": v(-86.83, -125.91) * mm, "end": v(-85.05, -125.05) * mm});
            skArc(sketch, "E29.25.4", {"start": v(-85.05, -125.05) * mm, "mid": v(-82.67, -124.71) * mm, "end": v(-80.39, -125.5) * mm});
            skArc(sketch, "E29.25.5", {"start": v(-77.6, -129.78) * mm, "mid": v(-78.31, -127.48) * mm, "end": v(-79.99, -125.75) * mm});
            skArc(sketch, "E29.25.6", {"start": v(-77.95, -133.72) * mm, "mid": v(-77.63, -131.76) * mm, "end": v(-77.6, -129.78) * mm});
            skLineSegment(sketch, "E29.25.7", {"start": v(-77.95, -133.72) * mm, "end": v(-78.2, -134.76) * mm});
            skLineSegment(sketch, "E29.25.8", {"start": v(-80.39, -125.5) * mm, "end": v(-80.19, -125.62) * mm});
            skLineSegment(sketch, "E29.25.9", {"start": v(-79.99, -125.75) * mm, "end": v(-80.19, -125.62) * mm});
            skArc(sketch, "E29.26.0", {"start": v(-63.93, -142.09) * mm, "mid": v(-63.96, -143.59) * mm, "end": v(-63.65, -145.06) * mm});
            skArc(sketch, "E29.26.1", {"start": v(-75.7, -136.2) * mm, "mid": v(-76.88, -137.13) * mm, "end": v(-78.24, -137.76) * mm});
            skLineSegment(sketch, "E29.26.2", {"start": v(-74.93, -135.45) * mm, "end": v(-75.7, -136.2) * mm});
            skArc(sketch, "E29.26.3", {"start": v(-74.93, -135.45) * mm, "mid": v(-73.42, -134.17) * mm, "end": v(-71.74, -133.13) * mm});
            skArc(sketch, "E29.26.4", {"start": v(-71.74, -133.13) * mm, "mid": v(-69.4, -132.55) * mm, "end": v(-67.06, -133.1) * mm});
            skArc(sketch, "E29.26.5", {"start": v(-63.85, -137.08) * mm, "mid": v(-64.79, -134.86) * mm, "end": v(-66.63, -133.3) * mm});
            skArc(sketch, "E29.26.6", {"start": v(-63.8, -141.02) * mm, "mid": v(-63.67, -139.05) * mm, "end": v(-63.85, -137.08) * mm});
            skLineSegment(sketch, "E29.26.7", {"start": v(-63.8, -141.02) * mm, "end": v(-63.93, -142.09) * mm});
            skLineSegment(sketch, "E29.26.8", {"start": v(-67.06, -133.1) * mm, "end": v(-66.85, -133.2) * mm});
            skLineSegment(sketch, "E29.26.9", {"start": v(-66.63, -133.3) * mm, "end": v(-66.85, -133.2) * mm});
            skArc(sketch, "E29.27.0", {"start": v(-48.99, -147.9) * mm, "mid": v(-48.86, -149.4) * mm, "end": v(-48.4, -150.83) * mm});
            skArc(sketch, "E29.27.1", {"start": v(-61.3, -143.27) * mm, "mid": v(-62.37, -144.3) * mm, "end": v(-63.66, -145.08) * mm});
            skLineSegment(sketch, "E29.27.2", {"start": v(-60.6, -142.44) * mm, "end": v(-61.3, -143.27) * mm});
            skArc(sketch, "E29.27.3", {"start": v(-60.6, -142.44) * mm, "mid": v(-59.24, -141.01) * mm, "end": v(-57.67, -139.8) * mm});
            skArc(sketch, "E29.27.4", {"start": v(-57.67, -139.8) * mm, "mid": v(-55.4, -138.99) * mm, "end": v(-53.02, -139.29) * mm});
            skArc(sketch, "E29.27.5", {"start": v(-49.42, -142.92) * mm, "mid": v(-50.58, -140.8) * mm, "end": v(-52.57, -139.45) * mm});
            skArc(sketch, "E29.27.6", {"start": v(-48.95, -146.83) * mm, "mid": v(-49.04, -144.86) * mm, "end": v(-49.42, -142.92) * mm});
            skLineSegment(sketch, "E29.27.7", {"start": v(-48.95, -146.83) * mm, "end": v(-48.99, -147.9) * mm});
            skLineSegment(sketch, "E29.27.8", {"start": v(-53.02, -139.29) * mm, "end": v(-52.8, -139.37) * mm});
            skLineSegment(sketch, "E29.27.9", {"start": v(-52.57, -139.45) * mm, "end": v(-52.8, -139.37) * mm});
            skArc(sketch, "E29.28.0", {"start": v(-33.52, -152.16) * mm, "mid": v(-33.24, -153.64) * mm, "end": v(-32.64, -155.01) * mm});
            skArc(sketch, "E29.28.1", {"start": v(-46.24, -148.81) * mm, "mid": v(-47.2, -149.96) * mm, "end": v(-48.4, -150.86) * mm});
            skLineSegment(sketch, "E29.28.2", {"start": v(-45.64, -147.92) * mm, "end": v(-46.24, -148.81) * mm});
            skArc(sketch, "E29.28.3", {"start": v(-45.64, -147.92) * mm, "mid": v(-44.42, -146.36) * mm, "end": v(-43, -145) * mm});
            skArc(sketch, "E29.28.4", {"start": v(-43, -145) * mm, "mid": v(-40.82, -143.95) * mm, "end": v(-38.42, -144) * mm});
            skArc(sketch, "E29.28.5", {"start": v(-34.46, -147.24) * mm, "mid": v(-35.83, -145.26) * mm, "end": v(-37.95, -144.12) * mm});
            skArc(sketch, "E29.28.6", {"start": v(-33.6, -151.09) * mm, "mid": v(-33.89, -149.13) * mm, "end": v(-34.46, -147.24) * mm});
            skLineSegment(sketch, "E29.28.7", {"start": v(-33.6, -151.09) * mm, "end": v(-33.52, -152.16) * mm});
            skLineSegment(sketch, "E29.28.8", {"start": v(-38.42, -144) * mm, "end": v(-38.19, -144.06) * mm});
            skLineSegment(sketch, "E29.28.9", {"start": v(-37.95, -144.12) * mm, "end": v(-38.19, -144.06) * mm});
            skArc(sketch, "E29.29.0", {"start": v(-17.7, -154.8) * mm, "mid": v(-17.27, -156.24) * mm, "end": v(-16.52, -157.54) * mm});
            skArc(sketch, "E29.29.1", {"start": v(-30.7, -152.78) * mm, "mid": v(-31.54, -154.02) * mm, "end": v(-32.64, -155.03) * mm});
            skLineSegment(sketch, "E29.29.2", {"start": v(-30.19, -151.83) * mm, "end": v(-30.7, -152.78) * mm});
            skArc(sketch, "E29.29.3", {"start": v(-30.19, -151.83) * mm, "mid": v(-29.14, -150.15) * mm, "end": v(-27.85, -148.65) * mm});
            skArc(sketch, "E29.29.4", {"start": v(-27.85, -148.65) * mm, "mid": v(-25.8, -147.38) * mm, "end": v(-23.4, -147.19) * mm});
            skArc(sketch, "E29.29.5", {"start": v(-19.14, -150) * mm, "mid": v(-20.7, -148.18) * mm, "end": v(-22.94, -147.26) * mm});
            skArc(sketch, "E29.29.6", {"start": v(-17.88, -153.74) * mm, "mid": v(-18.37, -151.83) * mm, "end": v(-19.14, -150) * mm});
            skLineSegment(sketch, "E29.29.7", {"start": v(-17.88, -153.74) * mm, "end": v(-17.7, -154.8) * mm});
            skLineSegment(sketch, "E29.29.8", {"start": v(-23.4, -147.19) * mm, "end": v(-23.17, -147.22) * mm});
            skLineSegment(sketch, "E29.29.9", {"start": v(-22.94, -147.26) * mm, "end": v(-23.17, -147.22) * mm});
            skArc(sketch, "E29.30.0", {"start": v(-1.68, -155.8) * mm, "mid": v(-1.11, -157.19) * mm, "end": v(-0.24, -158.4) * mm});
            skArc(sketch, "E29.30.1", {"start": v(-14.82, -155.12) * mm, "mid": v(-15.53, -156.44) * mm, "end": v(-16.53, -157.57) * mm});
            skLineSegment(sketch, "E29.30.2", {"start": v(-14.42, -154.12) * mm, "end": v(-14.82, -155.12) * mm});
            skArc(sketch, "E29.30.3", {"start": v(-14.42, -154.12) * mm, "mid": v(-13.55, -152.35) * mm, "end": v(-12.42, -150.72) * mm});
            skArc(sketch, "E29.30.4", {"start": v(-12.42, -150.72) * mm, "mid": v(-10.51, -149.25) * mm, "end": v(-8.15, -148.81) * mm});
            skArc(sketch, "E29.30.5", {"start": v(-3.62, -151.18) * mm, "mid": v(-5.36, -149.52) * mm, "end": v(-7.67, -148.84) * mm});
            skArc(sketch, "E29.30.6", {"start": v(-1.98, -154.77) * mm, "mid": v(-2.66, -152.9) * mm, "end": v(-3.62, -151.18) * mm});
            skLineSegment(sketch, "E29.30.7", {"start": v(-1.98, -154.77) * mm, "end": v(-1.68, -155.8) * mm});
            skLineSegment(sketch, "E29.30.8", {"start": v(-8.15, -148.81) * mm, "end": v(-7.9, -148.82) * mm});
            skLineSegment(sketch, "E29.30.9", {"start": v(-7.67, -148.84) * mm, "end": v(-7.9, -148.82) * mm});
            skArc(sketch, "E29.31.0", {"start": v(14.34, -155.15) * mm, "mid": v(15.06, -156.47) * mm, "end": v(16.05, -157.6) * mm});
            skArc(sketch, "E29.31.1", {"start": v(1.2, -155.82) * mm, "mid": v(0.64, -157.21) * mm, "end": v(-0.24, -158.43) * mm});
            skLineSegment(sketch, "E29.31.2", {"start": v(1.5, -154.8) * mm, "end": v(1.2, -155.82) * mm});
            skArc(sketch, "E29.31.3", {"start": v(1.5, -154.8) * mm, "mid": v(2.19, -152.93) * mm, "end": v(3.14, -151.2) * mm});
            skArc(sketch, "E29.31.4", {"start": v(3.14, -151.2) * mm, "mid": v(4.89, -149.54) * mm, "end": v(7.2, -148.86) * mm});
            skArc(sketch, "E29.31.5", {"start": v(11.95, -150.75) * mm, "mid": v(10.04, -149.28) * mm, "end": v(7.67, -148.84) * mm});
            skArc(sketch, "E29.31.6", {"start": v(13.94, -154.15) * mm, "mid": v(13.07, -152.37) * mm, "end": v(11.95, -150.75) * mm});
            skLineSegment(sketch, "E29.31.7", {"start": v(13.94, -154.15) * mm, "end": v(14.34, -155.15) * mm});
            skLineSegment(sketch, "E29.31.8", {"start": v(7.2, -148.86) * mm, "end": v(7.43, -148.85) * mm});
            skLineSegment(sketch, "E29.31.9", {"start": v(7.67, -148.84) * mm, "end": v(7.43, -148.85) * mm});
            skArc(sketch, "E29.32.0", {"start": v(30.22, -152.85) * mm, "mid": v(31.07, -154.1) * mm, "end": v(32.17, -155.1) * mm});
            skArc(sketch, "E29.32.1", {"start": v(17.22, -154.87) * mm, "mid": v(16.8, -156.31) * mm, "end": v(16.05, -157.62) * mm});
            skLineSegment(sketch, "E29.32.2", {"start": v(17.41, -153.82) * mm, "end": v(17.22, -154.87) * mm});
            skArc(sketch, "E29.32.3", {"start": v(17.41, -153.82) * mm, "mid": v(17.9, -151.9) * mm, "end": v(18.67, -150.08) * mm});
            skArc(sketch, "E29.32.4", {"start": v(18.67, -150.08) * mm, "mid": v(20.24, -148.25) * mm, "end": v(22.46, -147.33) * mm});
            skArc(sketch, "E29.32.5", {"start": v(27.38, -148.72) * mm, "mid": v(25.33, -147.45) * mm, "end": v(22.94, -147.26) * mm});
            skArc(sketch, "E29.32.6", {"start": v(29.72, -151.9) * mm, "mid": v(28.67, -150.22) * mm, "end": v(27.38, -148.72) * mm});
            skLineSegment(sketch, "E29.32.7", {"start": v(29.72, -151.9) * mm, "end": v(30.22, -152.85) * mm});
            skLineSegment(sketch, "E29.32.8", {"start": v(22.46, -147.33) * mm, "end": v(22.7, -147.3) * mm});
            skLineSegment(sketch, "E29.32.9", {"start": v(22.94, -147.26) * mm, "end": v(22.7, -147.3) * mm});
            skArc(sketch, "E29.33.0", {"start": v(45.78, -148.93) * mm, "mid": v(46.74, -150.08) * mm, "end": v(47.95, -150.98) * mm});
            skArc(sketch, "E29.33.1", {"start": v(33.06, -152.28) * mm, "mid": v(32.78, -153.76) * mm, "end": v(32.18, -155.13) * mm});
            skLineSegment(sketch, "E29.33.2", {"start": v(33.14, -151.2) * mm, "end": v(33.06, -152.28) * mm});
            skArc(sketch, "E29.33.3", {"start": v(33.14, -151.2) * mm, "mid": v(33.43, -149.25) * mm, "end": v(34, -147.36) * mm});
            skArc(sketch, "E29.33.4", {"start": v(34, -147.36) * mm, "mid": v(35.37, -145.38) * mm, "end": v(37.5, -144.24) * mm});
            skArc(sketch, "E29.33.5", {"start": v(42.53, -145.11) * mm, "mid": v(40.36, -144.07) * mm, "end": v(37.95, -144.12) * mm});
            skArc(sketch, "E29.33.6", {"start": v(45.18, -148.04) * mm, "mid": v(43.96, -146.48) * mm, "end": v(42.53, -145.11) * mm});
            skLineSegment(sketch, "E29.33.7", {"start": v(45.18, -148.04) * mm, "end": v(45.78, -148.93) * mm});
            skLineSegment(sketch, "E29.33.8", {"start": v(37.5, -144.24) * mm, "end": v(37.72, -144.18) * mm});
            skLineSegment(sketch, "E29.33.9", {"start": v(37.95, -144.12) * mm, "end": v(37.72, -144.18) * mm});
            skArc(sketch, "E29.34.0", {"start": v(60.85, -143.44) * mm, "mid": v(61.93, -144.48) * mm, "end": v(63.22, -145.25) * mm});
            skArc(sketch, "E29.34.1", {"start": v(48.54, -148.08) * mm, "mid": v(48.42, -149.57) * mm, "end": v(47.96, -151) * mm});
            skLineSegment(sketch, "E29.34.2", {"start": v(48.5, -147) * mm, "end": v(48.54, -148.08) * mm});
            skArc(sketch, "E29.34.3", {"start": v(48.5, -147) * mm, "mid": v(48.6, -145.02) * mm, "end": v(48.97, -143.08) * mm});
            skArc(sketch, "E29.34.4", {"start": v(48.97, -143.08) * mm, "mid": v(50.13, -140.97) * mm, "end": v(52.13, -139.62) * mm});
            skArc(sketch, "E29.34.5", {"start": v(57.23, -139.97) * mm, "mid": v(54.96, -139.15) * mm, "end": v(52.57, -139.45) * mm});
            skArc(sketch, "E29.34.6", {"start": v(60.16, -142.6) * mm, "mid": v(58.8, -141.18) * mm, "end": v(57.23, -139.97) * mm});
            skLineSegment(sketch, "E29.34.7", {"start": v(60.16, -142.6) * mm, "end": v(60.85, -143.44) * mm});
            skLineSegment(sketch, "E29.34.8", {"start": v(52.13, -139.62) * mm, "end": v(52.35, -139.54) * mm});
            skLineSegment(sketch, "E29.34.9", {"start": v(52.57, -139.45) * mm, "end": v(52.35, -139.54) * mm});
            skArc(sketch, "E29.35.0", {"start": v(75.27, -136.42) * mm, "mid": v(76.46, -137.34) * mm, "end": v(77.82, -137.98) * mm});
            skArc(sketch, "E29.35.1", {"start": v(63.5, -142.3) * mm, "mid": v(63.54, -143.8) * mm, "end": v(63.23, -145.27) * mm});
            skLineSegment(sketch, "E29.35.2", {"start": v(63.37, -141.23) * mm, "end": v(63.5, -142.3) * mm});
            skArc(sketch, "E29.35.3", {"start": v(63.37, -141.23) * mm, "mid": v(63.25, -139.26) * mm, "end": v(63.43, -137.29) * mm});
            skArc(sketch, "E29.35.4", {"start": v(63.43, -137.29) * mm, "mid": v(64.36, -135.07) * mm, "end": v(66.2, -133.52) * mm});
            skArc(sketch, "E29.35.5", {"start": v(71.31, -133.35) * mm, "mid": v(68.98, -132.77) * mm, "end": v(66.63, -133.3) * mm});
            skArc(sketch, "E29.35.6", {"start": v(74.5, -135.67) * mm, "mid": v(73, -134.39) * mm, "end": v(71.31, -133.35) * mm});
            skLineSegment(sketch, "E29.35.7", {"start": v(74.5, -135.67) * mm, "end": v(75.27, -136.42) * mm});
            skLineSegment(sketch, "E29.35.8", {"start": v(66.2, -133.52) * mm, "end": v(66.42, -133.42) * mm});
            skLineSegment(sketch, "E29.35.9", {"start": v(66.63, -133.3) * mm, "end": v(66.42, -133.42) * mm});
            skArc(sketch, "E29.36.0", {"start": v(88.9, -127.96) * mm, "mid": v(90.17, -128.76) * mm, "end": v(91.6, -129.24) * mm});
            skArc(sketch, "E29.36.1", {"start": v(77.8, -135.02) * mm, "mid": v(77.99, -136.5) * mm, "end": v(77.83, -138) * mm});
            skLineSegment(sketch, "E29.36.2", {"start": v(77.55, -133.97) * mm, "end": v(77.8, -135.02) * mm});
            skArc(sketch, "E29.36.3", {"start": v(77.55, -133.97) * mm, "mid": v(77.23, -132.02) * mm, "end": v(77.2, -130.04) * mm});
            skArc(sketch, "E29.36.4", {"start": v(77.2, -130.04) * mm, "mid": v(77.91, -127.74) * mm, "end": v(79.58, -126) * mm});
            skArc(sketch, "E29.36.5", {"start": v(84.65, -125.3) * mm, "mid": v(82.26, -124.97) * mm, "end": v(79.99, -125.75) * mm});
            skArc(sketch, "E29.36.6", {"start": v(88.06, -127.29) * mm, "mid": v(86.43, -126.17) * mm, "end": v(84.65, -125.3) * mm});
            skLineSegment(sketch, "E29.36.7", {"start": v(88.06, -127.29) * mm, "end": v(88.9, -127.96) * mm});
            skLineSegment(sketch, "E29.36.8", {"start": v(79.58, -126) * mm, "end": v(79.79, -125.88) * mm});
            skLineSegment(sketch, "E29.36.9", {"start": v(79.99, -125.75) * mm, "end": v(79.79, -125.88) * mm});
            skArc(sketch, "E29.37.0", {"start": v(101.59, -118.14) * mm, "mid": v(102.93, -118.8) * mm, "end": v(104.4, -119.14) * mm});
            skArc(sketch, "E29.37.1", {"start": v(91.27, -126.3) * mm, "mid": v(91.6, -127.76) * mm, "end": v(91.6, -129.26) * mm});
            skLineSegment(sketch, "E29.37.2", {"start": v(90.92, -125.29) * mm, "end": v(91.27, -126.3) * mm});
            skArc(sketch, "E29.37.3", {"start": v(90.92, -125.29) * mm, "mid": v(90.4, -123.38) * mm, "end": v(90.17, -121.41) * mm});
            skArc(sketch, "E29.37.4", {"start": v(90.17, -121.41) * mm, "mid": v(90.63, -119.05) * mm, "end": v(92.12, -117.16) * mm});
            skArc(sketch, "E29.37.5", {"start": v(97.08, -115.94) * mm, "mid": v(94.68, -115.85) * mm, "end": v(92.5, -116.86) * mm});
            skArc(sketch, "E29.37.6", {"start": v(100.68, -117.56) * mm, "mid": v(98.94, -116.61) * mm, "end": v(97.08, -115.94) * mm});
            skLineSegment(sketch, "E29.37.7", {"start": v(100.68, -117.56) * mm, "end": v(101.59, -118.14) * mm});
            skLineSegment(sketch, "E29.37.8", {"start": v(92.12, -117.16) * mm, "end": v(92.3, -117) * mm});
            skLineSegment(sketch, "E29.37.9", {"start": v(92.5, -116.86) * mm, "end": v(92.3, -117) * mm});
            skArc(sketch, "E29.38.0", {"start": v(113.2, -107.07) * mm, "mid": v(114.6, -107.59) * mm, "end": v(116.1, -107.78) * mm});
            skArc(sketch, "E29.38.1", {"start": v(103.78, -116.25) * mm, "mid": v(104.26, -117.67) * mm, "end": v(104.41, -119.16) * mm});
            skLineSegment(sketch, "E29.38.2", {"start": v(103.32, -115.27) * mm, "end": v(103.78, -116.25) * mm});
            skArc(sketch, "E29.38.3", {"start": v(103.32, -115.27) * mm, "mid": v(102.6, -113.43) * mm, "end": v(102.17, -111.5) * mm});
            skArc(sketch, "E29.38.4", {"start": v(102.17, -111.5) * mm, "mid": v(102.4, -109.1) * mm, "end": v(103.68, -107.06) * mm});
            skArc(sketch, "E29.38.5", {"start": v(108.49, -105.34) * mm, "mid": v(106.09, -105.5) * mm, "end": v(104.02, -106.73) * mm});
            skArc(sketch, "E29.38.6", {"start": v(112.24, -106.58) * mm, "mid": v(110.4, -105.82) * mm, "end": v(108.49, -105.34) * mm});
            skLineSegment(sketch, "E29.38.7", {"start": v(112.24, -106.58) * mm, "end": v(113.2, -107.07) * mm});
            skLineSegment(sketch, "E29.38.8", {"start": v(103.68, -107.06) * mm, "end": v(103.85, -106.9) * mm});
            skLineSegment(sketch, "E29.38.9", {"start": v(104.02, -106.73) * mm, "end": v(103.85, -106.9) * mm});
            skArc(sketch, "E29.39.0", {"start": v(123.6, -94.86) * mm, "mid": v(125.06, -95.23) * mm, "end": v(126.56, -95.27) * mm});
            skArc(sketch, "E29.39.1", {"start": v(115.18, -104.96) * mm, "mid": v(115.8, -106.32) * mm, "end": v(116.11, -107.8) * mm});
            skLineSegment(sketch, "E29.39.2", {"start": v(114.62, -104.04) * mm, "end": v(115.18, -104.96) * mm});
            skArc(sketch, "E29.39.3", {"start": v(114.62, -104.04) * mm, "mid": v(113.72, -102.28) * mm, "end": v(113.1, -100.4) * mm});
            skArc(sketch, "E29.39.4", {"start": v(113.1, -100.4) * mm, "mid": v(113.07, -98) * mm, "end": v(114.14, -95.84) * mm});
            skArc(sketch, "E29.39.5", {"start": v(118.75, -93.63) * mm, "mid": v(116.37, -94.03) * mm, "end": v(114.44, -95.47) * mm});
            skArc(sketch, "E29.39.6", {"start": v(122.6, -94.48) * mm, "mid": v(120.7, -93.9) * mm, "end": v(118.75, -93.63) * mm});
            skLineSegment(sketch, "E29.39.7", {"start": v(122.6, -94.48) * mm, "end": v(123.6, -94.86) * mm});
            skLineSegment(sketch, "E29.39.8", {"start": v(114.14, -95.84) * mm, "end": v(114.29, -95.65) * mm});
            skLineSegment(sketch, "E29.39.9", {"start": v(114.44, -95.47) * mm, "end": v(114.29, -95.65) * mm});
            skArc(sketch, "E29.40.0", {"start": v(132.7, -81.65) * mm, "mid": v(134.19, -81.87) * mm, "end": v(135.68, -81.75) * mm});
            skArc(sketch, "E29.40.1", {"start": v(125.36, -92.56) * mm, "mid": v(126.12, -93.85) * mm, "end": v(126.58, -95.28) * mm});
            skLineSegment(sketch, "E29.40.2", {"start": v(124.71, -91.7) * mm, "end": v(125.36, -92.56) * mm});
            skArc(sketch, "E29.40.3", {"start": v(124.71, -91.7) * mm, "mid": v(123.64, -90.04) * mm, "end": v(122.82, -88.24) * mm});
            skArc(sketch, "E29.40.4", {"start": v(122.82, -88.24) * mm, "mid": v(122.54, -85.85) * mm, "end": v(123.39, -83.6) * mm});
            skArc(sketch, "E29.40.5", {"start": v(127.74, -80.92) * mm, "mid": v(125.42, -81.57) * mm, "end": v(123.65, -83.2) * mm});
            skArc(sketch, "E29.40.6", {"start": v(131.66, -81.37) * mm, "mid": v(129.72, -81) * mm, "end": v(127.74, -80.92) * mm});
            skLineSegment(sketch, "E29.40.7", {"start": v(131.66, -81.37) * mm, "end": v(132.7, -81.65) * mm});
            skLineSegment(sketch, "E29.40.8", {"start": v(123.39, -83.6) * mm, "end": v(123.52, -83.4) * mm});
            skLineSegment(sketch, "E29.40.9", {"start": v(123.65, -83.2) * mm, "end": v(123.52, -83.4) * mm});
            skArc(sketch, "E29.41.0", {"start": v(140.4, -67.57) * mm, "mid": v(141.9, -67.64) * mm, "end": v(143.37, -67.37) * mm});
            skArc(sketch, "E29.41.1", {"start": v(134.21, -79.18) * mm, "mid": v(135.1, -80.39) * mm, "end": v(135.7, -81.76) * mm});
            skLineSegment(sketch, "E29.41.2", {"start": v(133.48, -78.4) * mm, "end": v(134.21, -79.18) * mm});
            skArc(sketch, "E29.41.3", {"start": v(133.48, -78.4) * mm, "mid": v(132.24, -76.85) * mm, "end": v(131.24, -75.14) * mm});
            skArc(sketch, "E29.41.4", {"start": v(131.24, -75.14) * mm, "mid": v(130.72, -72.8) * mm, "end": v(131.33, -70.46) * mm});
            skArc(sketch, "E29.41.5", {"start": v(135.39, -67.36) * mm, "mid": v(133.15, -68.24) * mm, "end": v(131.55, -70.04) * mm});
            skArc(sketch, "E29.41.6", {"start": v(139.33, -67.4) * mm, "mid": v(137.36, -67.23) * mm, "end": v(135.39, -67.36) * mm});
            skLineSegment(sketch, "E29.41.7", {"start": v(139.33, -67.4) * mm, "end": v(140.4, -67.57) * mm});
            skLineSegment(sketch, "E29.41.8", {"start": v(131.33, -70.46) * mm, "end": v(131.44, -70.25) * mm});
            skLineSegment(sketch, "E29.41.9", {"start": v(131.55, -70.04) * mm, "end": v(131.44, -70.25) * mm});
            skArc(sketch, "E29.42.0", {"start": v(146.6, -52.78) * mm, "mid": v(148.1, -52.7) * mm, "end": v(149.54, -52.27) * mm});
            skArc(sketch, "E29.42.1", {"start": v(141.64, -64.96) * mm, "mid": v(142.66, -66.07) * mm, "end": v(143.4, -67.38) * mm});
            skLineSegment(sketch, "E29.42.2", {"start": v(140.83, -64.25) * mm, "end": v(141.64, -64.96) * mm});
            skArc(sketch, "E29.42.3", {"start": v(140.83, -64.25) * mm, "mid": v(139.44, -62.85) * mm, "end": v(138.27, -61.25) * mm});
            skArc(sketch, "E29.42.4", {"start": v(138.27, -61.25) * mm, "mid": v(137.51, -58.97) * mm, "end": v(137.88, -56.59) * mm});
            skArc(sketch, "E29.42.5", {"start": v(141.6, -53.08) * mm, "mid": v(139.46, -54.19) * mm, "end": v(138.05, -56.15) * mm});
            skArc(sketch, "E29.42.6", {"start": v(145.52, -52.72) * mm, "mid": v(143.55, -52.75) * mm, "end": v(141.6, -53.08) * mm});
            skLineSegment(sketch, "E29.42.7", {"start": v(145.52, -52.72) * mm, "end": v(146.6, -52.78) * mm});
            skLineSegment(sketch, "E29.42.8", {"start": v(137.88, -56.59) * mm, "end": v(137.96, -56.37) * mm});
            skLineSegment(sketch, "E29.42.9", {"start": v(138.05, -56.15) * mm, "end": v(137.96, -56.37) * mm});
            skArc(sketch, "E29.43.0", {"start": v(151.25, -37.42) * mm, "mid": v(152.73, -37.18) * mm, "end": v(154.12, -36.62) * mm});
            skArc(sketch, "E29.43.1", {"start": v(147.57, -50.05) * mm, "mid": v(148.7, -51.05) * mm, "end": v(149.56, -52.28) * mm});
            skLineSegment(sketch, "E29.43.2", {"start": v(146.7, -49.43) * mm, "end": v(147.57, -50.05) * mm});
            skArc(sketch, "E29.43.3", {"start": v(146.7, -49.43) * mm, "mid": v(145.16, -48.18) * mm, "end": v(143.84, -46.7) * mm});
            skArc(sketch, "E29.43.4", {"start": v(143.84, -46.7) * mm, "mid": v(142.85, -44.51) * mm, "end": v(142.96, -42.11) * mm});
            skArc(sketch, "E29.43.5", {"start": v(146.3, -38.24) * mm, "mid": v(144.29, -39.56) * mm, "end": v(143.1, -41.65) * mm});
            skArc(sketch, "E29.43.6", {"start": v(150.17, -37.47) * mm, "mid": v(148.2, -37.71) * mm, "end": v(146.3, -38.24) * mm});
            skLineSegment(sketch, "E29.43.7", {"start": v(150.17, -37.47) * mm, "end": v(151.25, -37.42) * mm});
            skLineSegment(sketch, "E29.43.8", {"start": v(142.96, -42.11) * mm, "end": v(143.03, -41.88) * mm});
            skLineSegment(sketch, "E29.43.9", {"start": v(143.1, -41.65) * mm, "end": v(143.03, -41.88) * mm});
            skArc(sketch, "E29.44.0", {"start": v(154.3, -21.68) * mm, "mid": v(155.74, -21.28) * mm, "end": v(157.07, -20.58) * mm});
            skArc(sketch, "E29.44.1", {"start": v(151.94, -34.61) * mm, "mid": v(153.15, -35.5) * mm, "end": v(154.14, -36.62) * mm});
            skLineSegment(sketch, "E29.44.2", {"start": v(151, -34.09) * mm, "end": v(151.94, -34.61) * mm});
            skArc(sketch, "E29.44.3", {"start": v(151, -34.09) * mm, "mid": v(149.35, -33) * mm, "end": v(147.88, -31.67) * mm});
            skArc(sketch, "E29.44.4", {"start": v(147.88, -31.67) * mm, "mid": v(146.67, -29.6) * mm, "end": v(146.53, -27.19) * mm});
            skArc(sketch, "E29.44.5", {"start": v(149.46, -23) * mm, "mid": v(147.6, -24.52) * mm, "end": v(146.62, -26.72) * mm});
            skArc(sketch, "E29.44.6", {"start": v(153.23, -21.84) * mm, "mid": v(151.3, -22.28) * mm, "end": v(149.46, -23) * mm});
            skLineSegment(sketch, "E29.44.7", {"start": v(153.23, -21.84) * mm, "end": v(154.3, -21.68) * mm});
            skLineSegment(sketch, "E29.44.8", {"start": v(146.53, -27.19) * mm, "end": v(146.58, -26.95) * mm});
            skLineSegment(sketch, "E29.44.9", {"start": v(146.62, -26.72) * mm, "end": v(146.58, -26.95) * mm});
            skArc(sketch, "E29.45.0", {"start": v(155.7, -5.7) * mm, "mid": v(157.1, -5.16) * mm, "end": v(158.35, -4.32) * mm});
            skArc(sketch, "E29.45.1", {"start": v(154.69, -18.8) * mm, "mid": v(156, -19.56) * mm, "end": v(157.1, -20.58) * mm});
            skLineSegment(sketch, "E29.45.2", {"start": v(153.7, -18.38) * mm, "end": v(154.69, -18.8) * mm});
            skArc(sketch, "E29.45.3", {"start": v(153.7, -18.38) * mm, "mid": v(151.95, -17.47) * mm, "end": v(150.35, -16.3) * mm});
            skArc(sketch, "E29.45.4", {"start": v(150.35, -16.3) * mm, "mid": v(148.93, -14.35) * mm, "end": v(148.55, -11.98) * mm});
            skArc(sketch, "E29.45.5", {"start": v(151.03, -7.5) * mm, "mid": v(149.33, -9.21) * mm, "end": v(148.6, -11.5) * mm});
            skArc(sketch, "E29.45.6", {"start": v(154.66, -5.96) * mm, "mid": v(152.8, -6.6) * mm, "end": v(151.03, -7.5) * mm});
            skLineSegment(sketch, "E29.45.7", {"start": v(154.66, -5.96) * mm, "end": v(155.7, -5.7) * mm});
            skLineSegment(sketch, "E29.45.8", {"start": v(148.55, -11.98) * mm, "end": v(148.57, -11.74) * mm});
            skLineSegment(sketch, "E29.45.9", {"start": v(148.6, -11.5) * mm, "end": v(148.57, -11.74) * mm});
            skArc(sketch, "E29.46.0", {"start": v(155.46, 10.34) * mm, "mid": v(156.8, 11.02) * mm, "end": v(157.95, 11.99) * mm});
            skArc(sketch, "E29.46.1", {"start": v(155.8, -2.8) * mm, "mid": v(157.18, -3.41) * mm, "end": v(158.37, -4.32) * mm});
            skLineSegment(sketch, "E29.46.2", {"start": v(154.78, -2.48) * mm, "end": v(155.8, -2.8) * mm});
            skArc(sketch, "E29.46.3", {"start": v(154.78, -2.48) * mm, "mid": v(152.94, -1.75) * mm, "end": v(151.23, -0.75) * mm});
            skArc(sketch, "E29.46.4", {"start": v(151.23, -0.75) * mm, "mid": v(149.62, 1.04) * mm, "end": v(149, 3.36) * mm});
            skArc(sketch, "E29.46.5", {"start": v(151, 8.06) * mm, "mid": v(149.49, 6.2) * mm, "end": v(148.99, 3.84) * mm});
            skArc(sketch, "E29.46.6", {"start": v(154.46, 9.97) * mm, "mid": v(152.66, 9.14) * mm, "end": v(151, 8.06) * mm});
            skLineSegment(sketch, "E29.46.7", {"start": v(154.46, 9.97) * mm, "end": v(155.46, 10.34) * mm});
            skLineSegment(sketch, "E29.46.8", {"start": v(149, 3.36) * mm, "end": v(149, 3.6) * mm});
            skLineSegment(sketch, "E29.46.9", {"start": v(148.99, 3.84) * mm, "end": v(149, 3.6) * mm});
            skArc(sketch, "E29.47.0", {"start": v(153.58, 26.27) * mm, "mid": v(154.84, 27.09) * mm, "end": v(155.88, 28.17) * mm});
            skArc(sketch, "E29.47.1", {"start": v(155.27, 13.23) * mm, "mid": v(156.7, 12.77) * mm, "end": v(157.98, 12) * mm});
            skLineSegment(sketch, "E29.47.2", {"start": v(154.21, 13.45) * mm, "end": v(155.27, 13.23) * mm});
            skArc(sketch, "E29.47.3", {"start": v(154.21, 13.45) * mm, "mid": v(152.3, 13.98) * mm, "end": v(150.5, 14.8) * mm});
            skArc(sketch, "E29.47.4", {"start": v(150.5, 14.8) * mm, "mid": v(148.72, 16.41) * mm, "end": v(147.86, 18.66) * mm});
            skArc(sketch, "E29.47.5", {"start": v(149.37, 23.55) * mm, "mid": v(148.06, 21.53) * mm, "end": v(147.8, 19.14) * mm});
            skArc(sketch, "E29.47.6", {"start": v(152.61, 25.8) * mm, "mid": v(150.9, 24.8) * mm, "end": v(149.37, 23.55) * mm});
            skLineSegment(sketch, "E29.47.7", {"start": v(152.61, 25.8) * mm, "end": v(153.58, 26.27) * mm});
            skLineSegment(sketch, "E29.47.8", {"start": v(147.86, 18.66) * mm, "end": v(147.83, 18.9) * mm});
            skLineSegment(sketch, "E29.47.9", {"start": v(147.8, 19.14) * mm, "end": v(147.83, 18.9) * mm});
            skArc(sketch, "E29.48.0", {"start": v(150.06, 41.93) * mm, "mid": v(151.23, 42.87) * mm, "end": v(152.16, 44.04) * mm});
            skArc(sketch, "E29.48.1", {"start": v(153.08, 29.13) * mm, "mid": v(154.55, 28.8) * mm, "end": v(155.9, 28.17) * mm});
            skLineSegment(sketch, "E29.48.2", {"start": v(152.01, 29.23) * mm, "end": v(153.08, 29.13) * mm});
            skArc(sketch, "E29.48.3", {"start": v(152.01, 29.23) * mm, "mid": v(150.06, 29.57) * mm, "end": v(148.19, 30.2) * mm});
            skArc(sketch, "E29.48.4", {"start": v(148.19, 30.2) * mm, "mid": v(146.24, 31.62) * mm, "end": v(145.16, 33.77) * mm});
            skArc(sketch, "E29.48.5", {"start": v(146.16, 38.78) * mm, "mid": v(145.06, 36.64) * mm, "end": v(145.05, 34.23) * mm});
            skArc(sketch, "E29.48.6", {"start": v(149.15, 41.35) * mm, "mid": v(147.56, 40.18) * mm, "end": v(146.16, 38.78) * mm});
            skLineSegment(sketch, "E29.48.7", {"start": v(149.15, 41.35) * mm, "end": v(150.06, 41.93) * mm});
            skLineSegment(sketch, "E29.48.8", {"start": v(145.16, 33.77) * mm, "end": v(145.1, 34) * mm});
            skLineSegment(sketch, "E29.48.9", {"start": v(145.05, 34.23) * mm, "end": v(145.1, 34) * mm});
            skArc(sketch, "E29.49.0", {"start": v(144.96, 57.13) * mm, "mid": v(146.02, 58.19) * mm, "end": v(146.83, 59.46) * mm});
            skArc(sketch, "E29.49.1", {"start": v(149.28, 44.71) * mm, "mid": v(150.77, 44.55) * mm, "end": v(152.19, 44.05) * mm});
            skLineSegment(sketch, "E29.49.2", {"start": v(148.2, 44.7) * mm, "end": v(149.28, 44.71) * mm});
            skArc(sketch, "E29.49.3", {"start": v(148.2, 44.7) * mm, "mid": v(146.23, 44.84) * mm, "end": v(144.3, 45.27) * mm});
            skArc(sketch, "E29.49.4", {"start": v(144.3, 45.27) * mm, "mid": v(142.22, 46.49) * mm, "end": v(140.92, 48.51) * mm});
            skArc(sketch, "E29.49.5", {"start": v(141.4, 53.6) * mm, "mid": v(140.52, 51.36) * mm, "end": v(140.76, 48.96) * mm});
            skArc(sketch, "E29.49.6", {"start": v(144.1, 56.47) * mm, "mid": v(142.65, 55.14) * mm, "end": v(141.4, 53.6) * mm});
            skLineSegment(sketch, "E29.49.7", {"start": v(144.1, 56.47) * mm, "end": v(144.96, 57.13) * mm});
            skLineSegment(sketch, "E29.49.8", {"start": v(140.92, 48.51) * mm, "end": v(140.84, 48.74) * mm});
            skLineSegment(sketch, "E29.49.9", {"start": v(140.76, 48.96) * mm, "end": v(140.84, 48.74) * mm});
            skArc(sketch, "E29.50.0", {"start": v(138.31, 71.74) * mm, "mid": v(139.27, 72.9) * mm, "end": v(139.94, 74.24) * mm});
            skArc(sketch, "E29.50.1", {"start": v(143.89, 59.82) * mm, "mid": v(145.39, 59.81) * mm, "end": v(146.85, 59.47) * mm});
            skLineSegment(sketch, "E29.50.2", {"start": v(142.82, 59.7) * mm, "end": v(143.89, 59.82) * mm});
            skArc(sketch, "E29.50.3", {"start": v(142.82, 59.7) * mm, "mid": v(140.84, 59.64) * mm, "end": v(138.88, 59.87) * mm});
            skArc(sketch, "E29.50.4", {"start": v(138.88, 59.87) * mm, "mid": v(136.68, 60.86) * mm, "end": v(135.18, 62.75) * mm});
            skArc(sketch, "E29.50.5", {"start": v(135.14, 67.86) * mm, "mid": v(134.5, 65.54) * mm, "end": v(134.98, 63.18) * mm});
            skArc(sketch, "E29.50.6", {"start": v(137.54, 70.99) * mm, "mid": v(136.22, 69.51) * mm, "end": v(135.14, 67.86) * mm});
            skLineSegment(sketch, "E29.50.7", {"start": v(137.54, 70.99) * mm, "end": v(138.31, 71.74) * mm});
            skLineSegment(sketch, "E29.50.8", {"start": v(135.18, 62.75) * mm, "end": v(135.08, 62.96) * mm});
            skLineSegment(sketch, "E29.50.9", {"start": v(134.98, 63.18) * mm, "end": v(135.08, 62.96) * mm});
            skArc(sketch, "E29.51.0", {"start": v(130.2, 85.58) * mm, "mid": v(131.03, 86.83) * mm, "end": v(131.56, 88.23) * mm});
            skArc(sketch, "E29.51.1", {"start": v(136.97, 74.3) * mm, "mid": v(138.47, 74.45) * mm, "end": v(139.96, 74.25) * mm});
            skLineSegment(sketch, "E29.51.2", {"start": v(135.92, 74.08) * mm, "end": v(136.97, 74.3) * mm});
            skArc(sketch, "E29.51.3", {"start": v(135.92, 74.08) * mm, "mid": v(133.96, 73.8) * mm, "end": v(131.98, 73.83) * mm});
            skArc(sketch, "E29.51.4", {"start": v(131.98, 73.83) * mm, "mid": v(129.7, 74.6) * mm, "end": v(128.01, 76.31) * mm});
            skArc(sketch, "E29.51.5", {"start": v(127.45, 81.4) * mm, "mid": v(127.05, 79.02) * mm, "end": v(127.77, 76.72) * mm});
            skArc(sketch, "E29.51.6", {"start": v(129.51, 84.75) * mm, "mid": v(128.35, 83.15) * mm, "end": v(127.45, 81.4) * mm});
            skLineSegment(sketch, "E29.51.7", {"start": v(129.51, 84.75) * mm, "end": v(130.2, 85.58) * mm});
            skLineSegment(sketch, "E29.51.8", {"start": v(128.01, 76.31) * mm, "end": v(127.9, 76.52) * mm});
            skLineSegment(sketch, "E29.51.9", {"start": v(127.77, 76.72) * mm, "end": v(127.9, 76.52) * mm});
            skArc(sketch, "E29.52.0", {"start": v(120.71, 98.51) * mm, "mid": v(121.41, 99.84) * mm, "end": v(121.8, 101.3) * mm});
            skArc(sketch, "E29.52.1", {"start": v(128.6, 88) * mm, "mid": v(130.08, 88.29) * mm, "end": v(131.58, 88.25) * mm});
            skLineSegment(sketch, "E29.52.2", {"start": v(127.59, 87.66) * mm, "end": v(128.6, 88) * mm});
            skArc(sketch, "E29.52.3", {"start": v(127.59, 87.66) * mm, "mid": v(125.66, 87.2) * mm, "end": v(123.7, 87.01) * mm});
            skArc(sketch, "E29.52.4", {"start": v(123.7, 87.01) * mm, "mid": v(121.34, 87.54) * mm, "end": v(119.49, 89.07) * mm});
            skArc(sketch, "E29.52.5", {"start": v(118.4, 94.07) * mm, "mid": v(118.25, 91.66) * mm, "end": v(119.2, 89.45) * mm});
            skArc(sketch, "E29.52.6", {"start": v(120.11, 97.62) * mm, "mid": v(119.12, 95.9) * mm, "end": v(118.4, 94.07) * mm});
            skLineSegment(sketch, "E29.52.7", {"start": v(120.11, 97.62) * mm, "end": v(120.71, 98.51) * mm});
            skLineSegment(sketch, "E29.52.8", {"start": v(119.49, 89.07) * mm, "end": v(119.35, 89.26) * mm});
            skLineSegment(sketch, "E29.52.9", {"start": v(119.2, 89.45) * mm, "end": v(119.35, 89.26) * mm});
            skArc(sketch, "E29.53.0", {"start": v(109.95, 110.4) * mm, "mid": v(110.5, 111.8) * mm, "end": v(110.73, 113.28) * mm});
            skArc(sketch, "E29.53.1", {"start": v(118.88, 100.75) * mm, "mid": v(120.31, 101.2) * mm, "end": v(121.8, 101.3) * mm});
            skLineSegment(sketch, "E29.53.2", {"start": v(117.9, 100.31) * mm, "end": v(118.88, 100.75) * mm});
            skArc(sketch, "E29.53.3", {"start": v(117.9, 100.31) * mm, "mid": v(116.03, 99.65) * mm, "end": v(114.1, 99.27) * mm});
            skArc(sketch, "E29.53.4", {"start": v(114.1, 99.27) * mm, "mid": v(111.7, 99.55) * mm, "end": v(109.7, 100.89) * mm});
            skArc(sketch, "E29.53.5", {"start": v(108.1, 105.74) * mm, "mid": v(108.2, 103.34) * mm, "end": v(109.37, 101.24) * mm});
            skArc(sketch, "E29.53.6", {"start": v(109.44, 109.45) * mm, "mid": v(108.63, 107.65) * mm, "end": v(108.1, 105.74) * mm});
            skLineSegment(sketch, "E29.53.7", {"start": v(109.44, 109.45) * mm, "end": v(109.95, 110.4) * mm});
            skLineSegment(sketch, "E29.53.8", {"start": v(109.7, 100.89) * mm, "end": v(109.54, 101.06) * mm});
            skLineSegment(sketch, "E29.53.9", {"start": v(109.37, 101.24) * mm, "end": v(109.54, 101.06) * mm});
            skArc(sketch, "E29.54.0", {"start": v(98.01, 121.12) * mm, "mid": v(98.42, 122.56) * mm, "end": v(98.5, 124.06) * mm});
            skArc(sketch, "E29.54.1", {"start": v(107.9, 112.44) * mm, "mid": v(109.27, 113.03) * mm, "end": v(110.75, 113.3) * mm});
            skLineSegment(sketch, "E29.54.2", {"start": v(106.96, 111.9) * mm, "end": v(107.9, 112.44) * mm});
            skArc(sketch, "E29.54.3", {"start": v(106.96, 111.9) * mm, "mid": v(105.17, 111.05) * mm, "end": v(103.28, 110.47) * mm});
            skArc(sketch, "E29.54.4", {"start": v(103.28, 110.47) * mm, "mid": v(100.87, 110.5) * mm, "end": v(98.74, 111.63) * mm});
            skArc(sketch, "E29.54.5", {"start": v(96.66, 116.3) * mm, "mid": v(97, 113.91) * mm, "end": v(98.39, 111.94) * mm});
            skArc(sketch, "E29.54.6", {"start": v(97.6, 120.13) * mm, "mid": v(96.99, 118.25) * mm, "end": v(96.66, 116.3) * mm});
            skLineSegment(sketch, "E29.54.7", {"start": v(97.6, 120.13) * mm, "end": v(98.01, 121.12) * mm});
            skLineSegment(sketch, "E29.54.8", {"start": v(98.74, 111.63) * mm, "end": v(98.56, 111.79) * mm});
            skLineSegment(sketch, "E29.54.9", {"start": v(98.39, 111.94) * mm, "end": v(98.56, 111.79) * mm});
            skArc(sketch, "E29.55.0", {"start": v(85.04, 130.56) * mm, "mid": v(85.3, 132.03) * mm, "end": v(85.22, 133.53) * mm});
            skArc(sketch, "E29.55.1", {"start": v(95.76, 122.94) * mm, "mid": v(97.07, 123.67) * mm, "end": v(98.51, 124.08) * mm});
            skLineSegment(sketch, "E29.55.2", {"start": v(94.88, 122.3) * mm, "end": v(95.76, 122.94) * mm});
            skArc(sketch, "E29.55.3", {"start": v(94.88, 122.3) * mm, "mid": v(93.2, 121.28) * mm, "end": v(91.37, 120.5) * mm});
            skArc(sketch, "E29.55.4", {"start": v(91.37, 120.5) * mm, "mid": v(88.98, 120.3) * mm, "end": v(86.74, 121.2) * mm});
            skArc(sketch, "E29.55.5", {"start": v(84.19, 125.62) * mm, "mid": v(84.77, 123.28) * mm, "end": v(86.35, 121.47) * mm});
            skArc(sketch, "E29.55.6", {"start": v(84.73, 129.52) * mm, "mid": v(84.31, 127.6) * mm, "end": v(84.19, 125.62) * mm});
            skLineSegment(sketch, "E29.55.7", {"start": v(84.73, 129.52) * mm, "end": v(85.04, 130.56) * mm});
            skLineSegment(sketch, "E29.55.8", {"start": v(86.74, 121.2) * mm, "end": v(86.55, 121.33) * mm});
            skLineSegment(sketch, "E29.55.9", {"start": v(86.35, 121.47) * mm, "end": v(86.55, 121.33) * mm});
            skArc(sketch, "E29.56.0", {"start": v(71.16, 138.6) * mm, "mid": v(71.27, 140.1) * mm, "end": v(71.04, 141.59) * mm});
            skArc(sketch, "E29.56.1", {"start": v(82.6, 132.13) * mm, "mid": v(83.84, 133) * mm, "end": v(85.23, 133.55) * mm});
            skLineSegment(sketch, "E29.56.2", {"start": v(81.8, 131.42) * mm, "end": v(82.6, 132.13) * mm});
            skArc(sketch, "E29.56.3", {"start": v(81.8, 131.42) * mm, "mid": v(80.23, 130.22) * mm, "end": v(78.5, 129.26) * mm});
            skArc(sketch, "E29.56.4", {"start": v(78.5, 129.26) * mm, "mid": v(76.14, 128.8) * mm, "end": v(73.82, 129.47) * mm});
            skArc(sketch, "E29.56.5", {"start": v(70.82, 133.6) * mm, "mid": v(71.65, 131.35) * mm, "end": v(73.4, 129.7) * mm});
            skArc(sketch, "E29.56.6", {"start": v(70.97, 137.55) * mm, "mid": v(70.75, 135.58) * mm, "end": v(70.82, 133.6) * mm});
            skLineSegment(sketch, "E29.56.7", {"start": v(70.97, 137.55) * mm, "end": v(71.16, 138.6) * mm});
            skLineSegment(sketch, "E29.56.8", {"start": v(73.82, 129.47) * mm, "end": v(73.61, 129.59) * mm});
            skLineSegment(sketch, "E29.56.9", {"start": v(73.4, 129.7) * mm, "end": v(73.61, 129.59) * mm});
            skArc(sketch, "E29.57.0", {"start": v(56.53, 145.19) * mm, "mid": v(56.49, 146.7) * mm, "end": v(56.1, 148.14) * mm});
            skArc(sketch, "E29.57.1", {"start": v(68.59, 139.92) * mm, "mid": v(69.72, 140.9) * mm, "end": v(71.05, 141.6) * mm});
            skLineSegment(sketch, "E29.57.2", {"start": v(67.86, 139.13) * mm, "end": v(68.59, 139.92) * mm});
            skArc(sketch, "E29.57.3", {"start": v(67.86, 139.13) * mm, "mid": v(66.42, 137.78) * mm, "end": v(64.8, 136.65) * mm});
            skArc(sketch, "E29.57.4", {"start": v(64.8, 136.65) * mm, "mid": v(62.49, 135.95) * mm, "end": v(60.12, 136.37) * mm});
            skArc(sketch, "E29.57.5", {"start": v(56.71, 140.18) * mm, "mid": v(57.76, 138.02) * mm, "end": v(59.68, 136.56) * mm});
            skArc(sketch, "E29.57.6", {"start": v(56.45, 144.12) * mm, "mid": v(56.43, 142.14) * mm, "end": v(56.71, 140.18) * mm});
            skLineSegment(sketch, "E29.57.7", {"start": v(56.45, 144.12) * mm, "end": v(56.53, 145.19) * mm});
            skLineSegment(sketch, "E29.57.8", {"start": v(60.12, 136.37) * mm, "end": v(59.9, 136.47) * mm});
            skLineSegment(sketch, "E29.57.9", {"start": v(59.68, 136.56) * mm, "end": v(59.9, 136.47) * mm});
            skArc(sketch, "E29.58.0", {"start": v(41.3, 150.23) * mm, "mid": v(41.1, 151.72) * mm, "end": v(40.57, 153.12) * mm});
            skArc(sketch, "E29.58.1", {"start": v(53.84, 146.23) * mm, "mid": v(54.86, 147.33) * mm, "end": v(56.1, 148.16) * mm});
            skLineSegment(sketch, "E29.58.2", {"start": v(53.2, 145.37) * mm, "end": v(53.84, 146.23) * mm});
            skArc(sketch, "E29.58.3", {"start": v(53.2, 145.37) * mm, "mid": v(51.9, 143.87) * mm, "end": v(50.4, 142.59) * mm});
            skArc(sketch, "E29.58.4", {"start": v(50.4, 142.59) * mm, "mid": v(48.18, 141.65) * mm, "end": v(45.78, 141.83) * mm});
            skArc(sketch, "E29.58.5", {"start": v(42, 145.27) * mm, "mid": v(43.26, 143.22) * mm, "end": v(45.32, 141.98) * mm});
            skArc(sketch, "E29.58.6", {"start": v(41.33, 149.16) * mm, "mid": v(41.52, 147.19) * mm, "end": v(42, 145.27) * mm});
            skLineSegment(sketch, "E29.58.7", {"start": v(41.33, 149.16) * mm, "end": v(41.3, 150.23) * mm});
            skLineSegment(sketch, "E29.58.8", {"start": v(45.78, 141.83) * mm, "end": v(45.55, 141.9) * mm});
            skLineSegment(sketch, "E29.58.9", {"start": v(45.32, 141.98) * mm, "end": v(45.55, 141.9) * mm});
            skArc(sketch, "E29.59.0", {"start": v(25.64, 153.68) * mm, "mid": v(25.29, 155.14) * mm, "end": v(24.61, 156.48) * mm});
            skArc(sketch, "E29.59.1", {"start": v(38.51, 151) * mm, "mid": v(39.42, 152.19) * mm, "end": v(40.58, 153.15) * mm});
            skLineSegment(sketch, "E29.59.2", {"start": v(37.97, 150.07) * mm, "end": v(38.51, 151) * mm});
            skArc(sketch, "E29.59.3", {"start": v(37.97, 150.07) * mm, "mid": v(36.83, 148.45) * mm, "end": v(35.47, 147.01) * mm});
            skArc(sketch, "E29.59.4", {"start": v(35.47, 147.01) * mm, "mid": v(33.36, 145.86) * mm, "end": v(30.95, 145.79) * mm});
            skArc(sketch, "E29.59.5", {"start": v(26.84, 148.82) * mm, "mid": v(28.3, 146.91) * mm, "end": v(30.49, 145.88) * mm});
            skArc(sketch, "E29.59.6", {"start": v(25.77, 152.62) * mm, "mid": v(26.16, 150.68) * mm, "end": v(26.84, 148.82) * mm});
            skLineSegment(sketch, "E29.59.7", {"start": v(25.77, 152.62) * mm, "end": v(25.64, 153.68) * mm});
            skLineSegment(sketch, "E29.59.8", {"start": v(30.95, 145.79) * mm, "end": v(30.72, 145.83) * mm});
            skLineSegment(sketch, "E29.59.9", {"start": v(30.49, 145.88) * mm, "end": v(30.72, 145.83) * mm});
            skArc(sketch, "E29.60.0", {"start": v(9.7, 155.5) * mm, "mid": v(9.2, 156.92) * mm, "end": v(8.4, 158.19) * mm});
            skArc(sketch, "E29.60.1", {"start": v(22.78, 154.15) * mm, "mid": v(23.57, 155.44) * mm, "end": v(24.62, 156.5) * mm});
            skLineSegment(sketch, "E29.60.2", {"start": v(22.33, 153.18) * mm, "end": v(22.78, 154.15) * mm});
            skArc(sketch, "E29.60.3", {"start": v(22.33, 153.18) * mm, "mid": v(21.37, 151.45) * mm, "end": v(20.17, 149.88) * mm});
            skArc(sketch, "E29.60.4", {"start": v(20.17, 149.88) * mm, "mid": v(18.18, 148.51) * mm, "end": v(15.8, 148.2) * mm});
            skArc(sketch, "E29.60.5", {"start": v(11.4, 150.79) * mm, "mid": v(13.05, 149.04) * mm, "end": v(15.32, 148.24) * mm});
            skArc(sketch, "E29.60.6", {"start": v(9.94, 154.46) * mm, "mid": v(10.53, 152.57) * mm, "end": v(11.4, 150.79) * mm});
            skLineSegment(sketch, "E29.60.7", {"start": v(9.94, 154.46) * mm, "end": v(9.7, 155.5) * mm});
            skLineSegment(sketch, "E29.60.8", {"start": v(15.8, 148.2) * mm, "end": v(15.56, 148.22) * mm});
            skLineSegment(sketch, "E29.60.9", {"start": v(15.32, 148.24) * mm, "end": v(15.56, 148.22) * mm});
            skPoint(sketch, "E29.center", {"position": v(0, 0) * mm});
            skSolve(sketch);
        }
        {
            var Q0;
            {var subQ171=sQuery(id+"F2.wireOp",EDGE,"E15");Q0=makeQuery(id+"F2.imprint","IMPRINT",FACE,{"disambiguationData":[TD([[makeQuery(id+"F2.imprint","IMPRINT",EDGE,{"derivedFrom":subQ171}),1.0]])]});}
            extrude(context, id + "F3", {"entities" : qUnion([Q0]), "operationType" : NewBodyOperationType.INTERSECT, "endBound" : BoundingType.THROUGH_ALL, "oppositeDirection" : true, "depth" : 25 * mm, "offsetDistance" : 25 * mm});
        }
        {
            var Q0;
            Q0=qCreatedBy(makeId("Right.planeOp"),FACE);
            var sketch = newSketch(context, id + "F4", { "sketchPlane" : qUnion([Q0])});
            skLineSegment(sketch, "E30", {"start": v(0, 72.2) * mm, "end": v(0, -78.72) * mm, "construction": true});
            skLineSegment(sketch, "E31", {"start": v(-84.45, 0) * mm, "end": v(97.88, 0) * mm, "construction": true});
            skCircle(sketch, "E32", {"center": v(0, 0) * mm, "radius": 52 * mm, "construction": true});
            skCircle(sketch, "E33", {"center": v(0, 52) * mm, "radius": 5.25 * mm});
            skCircle(sketch, "E34.1.0", {"center": v(-45.03, 26) * mm, "radius": 5.25 * mm});
            skCircle(sketch, "E34.2.0", {"center": v(-45.03, -26) * mm, "radius": 5.25 * mm});
            skCircle(sketch, "E34.3.0", {"center": v(0, -52) * mm, "radius": 5.25 * mm});
            skCircle(sketch, "E34.4.0", {"center": v(45.03, -26) * mm, "radius": 5.25 * mm});
            skCircle(sketch, "E34.5.0", {"center": v(45.03, 26) * mm, "radius": 5.25 * mm});
            skSolve(sketch);
        }
        {
            var Q0;
            Q0=makeQuery(id+"F4.imprint","IMPRINT",FACE,{"disambiguationData":[TD([[makeQuery(id+"F4.imprint","IMPRINT",EDGE,{"derivedFrom":sQuery(id+"F4.wireOp",EDGE,"E34.5.0")}),1.0]])]});
            var Q1;
            Q1=makeQuery(id+"F4.imprint","IMPRINT",FACE,{"disambiguationData":[TD([[makeQuery(id+"F4.imprint","IMPRINT",EDGE,{"derivedFrom":sQuery(id+"F4.wireOp",EDGE,"E33")}),1.0]])]});
            var Q2;
            Q2=makeQuery(id+"F4.imprint","IMPRINT",FACE,{"disambiguationData":[TD([[makeQuery(id+"F4.imprint","IMPRINT",EDGE,{"derivedFrom":sQuery(id+"F4.wireOp",EDGE,"E34.4.0")}),1.0]])]});
            var Q3;
            Q3=makeQuery(id+"F4.imprint","IMPRINT",FACE,{"disambiguationData":[TD([[makeQuery(id+"F4.imprint","IMPRINT",EDGE,{"derivedFrom":sQuery(id+"F4.wireOp",EDGE,"E34.3.0")}),1.0]])]});
            var Q4;
            Q4=makeQuery(id+"F4.imprint","IMPRINT",FACE,{"disambiguationData":[TD([[makeQuery(id+"F4.imprint","IMPRINT",EDGE,{"derivedFrom":sQuery(id+"F4.wireOp",EDGE,"E34.2.0")}),1.0]])]});
            var Q5;
            Q5=makeQuery(id+"F4.imprint","IMPRINT",FACE,{"disambiguationData":[TD([[makeQuery(id+"F4.imprint","IMPRINT",EDGE,{"derivedFrom":sQuery(id+"F4.wireOp",EDGE,"E34.1.0")}),1.0]])]});
            var Q6;
            Q6=sQuery(id+"F4.wireOp",EDGE,"E34.1.0");
            var Q7;
            Q7=sQuery(id+"F4.wireOp",EDGE,"E33");
            var Q8;
            Q8=sQuery(id+"F4.wireOp",EDGE,"E34.5.0");
            var Q9;
            Q9=sQuery(id+"F4.wireOp",EDGE,"E34.4.0");
            var Q10;
            Q10=sQuery(id+"F4.wireOp",EDGE,"E34.3.0");
            var Q11;
            Q11=sQuery(id+"F4.wireOp",EDGE,"E34.2.0");
            extrude(context, id + "F5", {"entities" : qUnion([Q0, Q1, Q2, Q3, Q4, Q5]), "operationType" : NewBodyOperationType.REMOVE, "surfaceEntities" : qUnion([Q6, Q7, Q8, Q9, Q10, Q11]), "depth" : 25 * mm, "offsetDistance" : 25 * mm});
        }
        {
            var Q0;
            Q0=makeQuery(id+"F1.opRevolve","SWEPT_FACE",FACE,{"disambiguationData":[OSD([sQuery(id+"F0.wireOp",EDGE,"E1.right")])]});
            var Q1;
            Q1=makeQuery(id+"F1.opRevolve","SWEPT_FACE",FACE,{"disambiguationData":[OSD([sQuery(id+"F0.wireOp",EDGE,"E1.left")])]});
            chamfer(context, id + "F6", {"entities" : qUnion([Q0, Q1]), "width" : 1 * mm, "tangentPropagation" : true});
        }
    });
